FCSTD DOCUMENT  (FreeCAD 0.19R24291 (Git))
Label: drawer
License: All rights reserved
LicenseURL: http://en.wikipedia.org/wiki/All_rights_reserved
objects: App::Link×7, App::DocumentObjectGroup×2, PartDesign::CoordinateSystem×2, App::FeaturePython×2, App::Part×1
note: 2 computed .brp shape members not serialized (recipe doc carries the construction recipe); baked Part::Feature solids carry a one-line shape summary decoded from their .brp
EXTERNAL_REF file=InnerFrontWall.FCStd obj=LCS_0
EXTERNAL_REF file=InnerFrontWall.FCStd obj=InnerFrontWall
EXTERNAL_REF file=InnerFrontWall.FCStd obj=InnerFrontWall_InnerRightWall_
EXTERNAL_REF file=InnerRightWall.FCStd obj=LCS_0
EXTERNAL_REF file=InnerRightWall.FCStd obj=InnerRightWall
EXTERNAL_REF file=InnerFrontWall.FCStd obj=InnerFrontWall_OuterRightWall
EXTERNAL_REF file=OuterRightWall.FCStd obj=LCS_0
EXTERNAL_REF file=OuterRightWall.FCStd obj=OuterRightWall
EXTERNAL_REF file=BackWall.FCStd obj=LCS_0
EXTERNAL_REF file=BackWall.FCStd obj=BackWall
EXTERNAL_REF file=Bottom.FCStd obj=LCS_0
EXTERNAL_REF file=InnerFrontWall.FCStd obj=InnerFrontWall_Bottom
EXTERNAL_REF file=Bottom.FCStd obj=Bottom
EXTERNAL_REF file=InnerFrontWall.FCStd obj=InnerFrontWall_OuterFrontWall
EXTERNAL_REF file=OuterFrontWall.FCStd obj=LCS_0
EXTERNAL_REF file=OuterFrontWall.FCStd obj=OuterFrontWall
EXTERNAL_REF file=FrontWindow.FCStd obj=LCS_0
EXTERNAL_REF file=OuterFrontWall.FCStd obj=OuterFrontWall_FrontWindow
EXTERNAL_REF file=FrontWindow.FCStd obj=FrontWindow

FEATURE [App::DocumentObjectGroup] Parts
FEATURE [PartDesign::CoordinateSystem] LCS_Origin
  AttacherType = Attacher::AttachEngine3D
  MapMode = 2
  Support = -> [X_Axis]
FEATURE [App::DocumentObjectGroup] Constraints
FEATURE [App::FeaturePython] Variables  # WARN: FeaturePython — macro-defined, semantics opaque (R4)
FEATURE [App::Link] InnerFrontWall_InnerFrontWall
  AssemblyType = Asm4EE
  AttachedBy = #LCS_0
  AttachedTo = Parent Assembly#LCS_Origin
  LinkedObject = -> <external InnerFrontWall.FCStd>#InnerFrontWall
  expr: Placement = LCS_Origin.Placement * AttachmentOffset * InnerFrontWall#LCS_0.Placement ^ -1
FEATURE [App::Link] InnerRightWall_InnerRightWall
  AssemblyType = Asm4EE
  AttachedBy = #LCS_0
  AttachedTo = InnerFrontWall_InnerFrontWall#InnerFrontWall_InnerRightWall_
  LinkPlacement = pos=(380.8,-7.5,0) rot=(0,0,1;0rad)
  LinkedObject = -> <external InnerRightWall.FCStd>#InnerRightWall
  Placement = pos=(380.8,-7.5,0) rot=(0,0,1;0rad)
  expr: Placement = InnerFrontWall_InnerFrontWall.Placement * InnerFrontWall#InnerFrontWall_InnerRightWall_.Placement * AttachmentOffset * InnerRightWall#LCS_0.Placement ^ -1
FEATURE [App::Link] OuterRightWall_OuterRightWall
  AssemblyType = Asm4EE
  AttachedBy = #LCS_0
  AttachedTo = InnerFrontWall_InnerFrontWall#InnerFrontWall_OuterRightWall
  LinkPlacement = pos=(395.8,-7.5,0) rot=(0,0,1;0rad)
  LinkedObject = -> <external OuterRightWall.FCStd>#OuterRightWall
  Placement = pos=(395.8,-7.5,0) rot=(0,0,1;0rad)
  expr: Placement = InnerFrontWall_InnerFrontWall.Placement * InnerFrontWall#InnerFrontWall_OuterRightWall.Placement * AttachmentOffset * OuterRightWall#LCS_0.Placement ^ -1
FEATURE [PartDesign::CoordinateSystem] Temp_Back
  AttacherType = Attacher::AttachEngine3D
  AttachmentOffset = pos=(7.5,350.8,0) rot=(0,0,1;0rad)
  MapMode = 2
  Placement = pos=(7.5,350.8,0) rot=(0,0,1;0rad)
  Support = -> [LCS_Origin]
  expr: .AttachmentOffset.Base.x = <<Attributes>>.WallThickness_WT / 2
  expr: .AttachmentOffset.Base.y = <<Attributes>>.InnerWallDepth - <<Attributes>>.WallThickness_WT / 2
FEATURE [App::FeaturePython] PropertyBag  label="Attributes"  # WARN: FeaturePython — macro-defined, semantics opaque (R4)
  BackWidth = 395.8
  Back_Space = 104
  BottomDepth = 365.8
  BottomWidth = 365.8
  Bottom_Height_BH = 4
  Bottom_Space_Height = 20
  Box_Tolerance = 0.2
  Boxes_Depth = 5
  Boxes_Height = 40
  Boxes_Width = 5
  CableChannelHight = 15
  CableChannelRadius = 2
  CustomPropertyGroups = shape | attributes
  DrawerDepth_DD = 469.8
  DrawerHeight_DH = 64
  DrawerWidth_DW = 410.8
  InnerWallDepth = 358.3
  LogicBoardScrewHeadDiameter = 6
  LogicBoardScrewHeadHeight = 3
  LogicBoardStandoffHoleDiameter = 3
  LogicBoardStandoffHoleSideSpace = 6
  LogicSpaceCornerRadius = 2
  LogicSpaceWidth = 100
  ScrewPreWhole = 3
  ScrewPreWholeDepth = 20
  SideLengt = 20
  WallThickness_WT = 15
  expr: InnerWallDepth = Boxes_Depth * 70mm + WallThickness_WT * 0.5 + Box_Tolerance * (Boxes_Width - 1)
  expr: DrawerDepth_DD = Boxes_Depth * 70mm + WallThickness_WT + Back_Space + Box_Tolerance * (Boxes_Width - 1)
  expr: BottomWidth = Boxes_Width * 70mm + WallThickness_WT + Box_Tolerance * (Boxes_Width - 1)
  expr: DrawerWidth_DW = Boxes_Width * 70mm + WallThickness_WT * 4 + Box_Tolerance * (Boxes_Width - 1)
  expr: BackWidth = DrawerWidth_DW - WallThickness_WT
  expr: DrawerHeight_DH = Boxes_Height + Bottom_Height_BH + Bottom_Space_Height
  expr: BottomDepth = Boxes_Depth * 70mm + WallThickness_WT + Box_Tolerance * (Boxes_Width - 1)
FEATURE [App::Link] BackWall_BackWall
  AssemblyType = Asm4EE
  AttachedBy = #LCS_0
  AttachedTo = Parent Assembly#Temp_Back
  LinkPlacement = pos=(7.5,350.8,0) rot=(0,0,1;0rad)
  LinkedObject = -> <external BackWall.FCStd>#BackWall
  Placement = pos=(7.5,350.8,0) rot=(0,0,1;0rad)
  expr: Placement = Temp_Back.Placement * AttachmentOffset * BackWall#LCS_0.Placement ^ -1
FEATURE [App::Link] Bottom_Bottom
  AssemblyType = Asm4EE
  AttachedBy = #LCS_0
  AttachedTo = InnerFrontWall_InnerFrontWall#InnerFrontWall_Bottom
  LinkPlacement = pos=(22.5,-7.5,20) rot=(0,0,1;0rad)
  LinkedObject = -> <external Bottom.FCStd>#Bottom
  Placement = pos=(22.5,-7.5,20) rot=(0,0,1;0rad)
  expr: Placement = InnerFrontWall_InnerFrontWall.Placement * InnerFrontWall#InnerFrontWall_Bottom.Placement * AttachmentOffset * Bottom#LCS_0.Placement ^ -1
FEATURE [App::Link] OuterFrontWall_OuterFrontWall
  AssemblyType = Asm4EE
  AttachedBy = #LCS_0
  AttachedTo = InnerFrontWall_InnerFrontWall#InnerFrontWall_OuterFrontWall
  LinkPlacement = pos=(-20,-15,8.3e-15) rot=(0,0,1;0rad)
  LinkedObject = -> <external OuterFrontWall.FCStd>#OuterFrontWall
  Placement = pos=(-20,-15,8.3e-15) rot=(0,0,1;0rad)
  expr: Placement = InnerFrontWall_InnerFrontWall.Placement * InnerFrontWall#InnerFrontWall_OuterFrontWall.Placement * AttachmentOffset * OuterFrontWall#LCS_0.Placement ^ -1
FEATURE [App::Link] FrontWindow_FrontWindow
  AssemblyType = Asm4EE
  AttachedBy = #LCS_0
  AttachedTo = OuterFrontWall_OuterFrontWall#OuterFrontWall_FrontWindow
  LinkPlacement = pos=(329.8,-30,32) rot=(0,0,1;0rad)
  LinkedObject = -> <external FrontWindow.FCStd>#FrontWindow
  Placement = pos=(329.8,-30,32) rot=(0,0,1;0rad)
  expr: Placement = OuterFrontWall_OuterFrontWall.Placement * OuterFrontWall#OuterFrontWall_FrontWindow.Placement * AttachmentOffset * FrontWindow#LCS_0.Placement ^ -1
FEATURE [App::Part] Model
  Configuration = 0
  Group = -> [LCS_Origin,Constraints,Variables,InnerFrontWall_InnerFrontWall,InnerRightWall_InnerRightWall,OuterRightWall_OuterRightWall,Temp_Back,PropertyBag,BackWall_BackWall,Bottom_Bottom,OuterFrontWall_OuterFrontWall,FrontWindow_FrontWindow]
  Origin = -> Origin
  Type = Assembly4 Model

RESOLVED EXTERNAL PARTS (link-assembly join: the EXTERNAL_REF files above that resolve inside this repo's crawl, each included once):
---- part BackWall.FCStd = doc fcstd_9a13f263e70f ----
FCSTD DOCUMENT  (FreeCAD 0.19R24291 (Git))
Label: BackWall
License: All rights reserved
LicenseURL: http://en.wikipedia.org/wiki/All_rights_reserved
objects: Sketcher::SketchObject×6, PartDesign::Pocket×5, PartDesign::CoordinateSystem×2, PartDesign::Pad×1, App::FeaturePython×1, PartDesign::Body×1, App::Part×1
note: 21 computed .brp shape members not serialized (recipe doc carries the construction recipe); baked Part::Feature solids carry a one-line shape summary decoded from their .brp

FEATURE [PartDesign::CoordinateSystem] LCS_0
  AttacherType = Attacher::AttachEngine3D
  MapMode = 2
  Support = -> [X_Axis]
FEATURE [PartDesign::CoordinateSystem] LCS_0001
  AttacherType = Attacher::AttachEngine3D
  MapMode = 2
  Support = -> [X_Axis001]
FEATURE [Sketcher::SketchObject] Sketch
  FullyConstrained = true
  MapMode = 5
  Placement = pos=(0,0,0) rot=(1,0,0;1.5708rad)
  Support = -> [XZ_Plane001]
  expr: Constraints[9] = <<Attributes>>.BackWidth
  expr: Constraints[10] = <<Attributes>>.DrawerHeight_DH
  sketch-geometry (4):
    g0: LineSegment StartX=0 StartY=0 StartZ=0 EndX=395.8 EndY=0 EndZ=0
    g1: LineSegment StartX=395.8 StartY=0 StartZ=0 EndX=395.8 EndY=64 EndZ=0
    g2: LineSegment StartX=395.8 StartY=64 StartZ=0 EndX=0 EndY=64 EndZ=0
    g3: LineSegment StartX=0 StartY=64 StartZ=0 EndX=0 EndY=0 EndZ=0
  constraints (11):
    c: Coincident(g0,g1)
    c: Coincident(g1,g2)
    c: Coincident(g2,g3)
    c: Coincident(g3,g0)
    c: Horizontal(g0)
    c: Horizontal(g2)
    c: Vertical(g1)
    c: Vertical(g3)
    c: Coincident(g0,g-1)
    c: Distance(g2) = 395.8
    c: Distance(g3) = 64
FEATURE [PartDesign::Pad] Pad
  Direction = (1,1,1)
  Length = 15
  Length2 = 100
  Placement = pos=(0,0,0) rot=(1,0,0;1.5708rad)
  Profile = -> Sketch
  Reversed = true
  Type = 0
  expr: Length = <<Attributes>>.WallThickness_WT
FEATURE [Sketcher::SketchObject] Sketch001
  FullyConstrained = true
  MapMode = 5
  Placement = pos=(0,-1e-16,0) rot=(1,0,0;1.5708rad)
  Support = -> [Pad]
  expr: Constraints[2] = <<Attributes>>.WallThickness_WT * 1
  expr: Constraints[3] = <<Attributes>>.BackWidth - <<Attributes>>.WallThickness_WT * 2
  expr: Constraints[28] = <<Attributes>>.Bottom_Space_Height / 2
  expr: Constraints[21] = <<Attributes>>.ScrewPreWhole / 2
  expr: Constraints[14] = <<Attributes>>.DrawerHeight_DH - <<Attributes>>.WallThickness_WT - <<Attributes>>.Bottom_Space_Height - <<Attributes>>.Bottom_Height_BH
  expr: Constraints[33] = <<Attributes>>.DrawerHeight_DH - <<Attributes>>.WallThickness_WT / 2
  sketch-geometry (13):
    g0: LineSegment StartX=15 StartY=56.5 StartZ=0 EndX=380.8 EndY=56.5 EndZ=0
    g1: LineSegment StartX=380.8 StartY=31.5 StartZ=0 EndX=15 EndY=31.5 EndZ=0
    g2: LineSegment StartX=15 StartY=31.5 StartZ=0 EndX=15 EndY=44 EndZ=0
    g3: LineSegment StartX=15 StartY=44 StartZ=0 EndX=15 EndY=56.5 EndZ=0
    g4: LineSegment StartX=380.8 StartY=31.5 StartZ=0 EndX=380.8 EndY=44 EndZ=0
    g5: LineSegment StartX=380.8 StartY=44 StartZ=0 EndX=380.8 EndY=56.5 EndZ=0
    g6: Circle CenterX=15 CenterY=56.5 CenterZ=0 NormalX=0 NormalY=0 NormalZ=1 AngleXU=0 Radius=1.5
    g7: Circle CenterX=15 CenterY=31.5 CenterZ=0 NormalX=0 NormalY=0 NormalZ=1 AngleXU=0 Radius=1.5
    g8: Circle CenterX=380.8 CenterY=31.5 CenterZ=0 NormalX=0 NormalY=0 NormalZ=1 AngleXU=0 Radius=1.5
    g9: Circle CenterX=380.8 CenterY=56.5 CenterZ=0 NormalX=0 NormalY=0 NormalZ=1 AngleXU=0 Radius=1.5
    g10: LineSegment StartX=15 StartY=10 StartZ=0 EndX=380.8 EndY=10 EndZ=0
    g11: Circle CenterX=15 CenterY=10 CenterZ=0 NormalX=0 NormalY=0 NormalZ=1 AngleXU=0 Radius=1.5
    g12: Circle CenterX=380.8 CenterY=10 CenterZ=0 NormalX=0 NormalY=0 NormalZ=1 AngleXU=0 Radius=1.5
  constraints (34):
    c: Horizontal(g0)
    c: Horizontal(g1)
    c: DistanceX(g-1,g1) = 15
    c: Distance(g0) = 365.8
    c: Coincident(g1,g2)
    c: Vertical(g2)
    c: Coincident(g3,g0)
    c: Vertical(g3)
    c: Equal(g2,g3)
    c: Coincident(g1,g4)
    c: Vertical(g4)
    c: Coincident(g5,g0)
    c: Vertical(g5)
    c: Equal(g5,g4)
    c: Distance(g1,g0) = 25
    c: Coincident(g6,g0)
    c: Coincident(g7,g1)
    c: Coincident(g8,g1)
    c: Coincident(g9,g0)
    c: Equal(g9,g8)
    c: Equal(g8,g6)
    c: Radius(g6) = 1.5
    c: Coincident(g3,g2)
    c: Coincident(g4,g5)
    c: Equal(g7,g6)
    c: Horizontal(g10)
    c: Vertical(g7,g10)
    c: Equal(g10,g1)
    c: DistanceY(g-1,g10) = 10
    c: Coincident(g11,g10)
    c: Coincident(g12,g10)
    c: Equal(g8,g12)
    c: Equal(g12,g11)
    c: DistanceY(g-1,g6) = 56.5
FEATURE [PartDesign::Pocket] Pocket
  BaseFeature = -> Pad
  Length = 5
  Length2 = 100
  Placement = pos=(0,0,0) rot=(1,0,0;1.5708rad)
  Profile = -> Sketch001
  Type = 1
FEATURE [Sketcher::SketchObject] Sketch002
  FullyConstrained = true
  MapMode = 5
  Placement = pos=(0,-1e-16,0) rot=(1,0,0;1.5708rad)
  Support = -> [Pocket]
  expr: Constraints[9] = <<Attributes>>.BackWidth
  expr: Constraints[10] = <<Attributes>>.Bottom_Space_Height
  expr: Constraints[11] = <<Attributes>>.Bottom_Height_BH
  sketch-geometry (4):
    g0: LineSegment StartX=0 StartY=20 StartZ=0 EndX=395.8 EndY=20 EndZ=0
    g1: LineSegment StartX=395.8 StartY=20 StartZ=0 EndX=395.8 EndY=24 EndZ=0
    g2: LineSegment StartX=395.8 StartY=24 StartZ=0 EndX=0 EndY=24 EndZ=0
    g3: LineSegment StartX=0 StartY=24 StartZ=0 EndX=0 EndY=20 EndZ=0
  constraints (12):
    c: Coincident(g0,g1)
    c: Coincident(g1,g2)
    c: Coincident(g2,g3)
    c: Coincident(g3,g0)
    c: Horizontal(g0)
    c: Horizontal(g2)
    c: Vertical(g1)
    c: Vertical(g3)
    c: PointOnObject(g0,g-2)
    c: Distance(g2) = 395.8
    c: DistanceY(g-1,g0) = 20
    c: Distance(g3) = 4
FEATURE [PartDesign::Pocket] Pocket001
  BaseFeature = -> Pocket
  Length = 7.5
  Length2 = 100
  Placement = pos=(0,0,0) rot=(1,0,0;1.5708rad)
  Profile = -> Sketch002
  Type = 0
  expr: Length = <<Attributes>>.WallThickness_WT / 2
FEATURE [Sketcher::SketchObject] Sketch003
  FullyConstrained = true
  MapMode = 5
  Placement = pos=(395.8,0,0) rot=(0.707107,0,0.707107;3.14159rad)
  Support = -> [Pocket001]
  expr: Constraints[3] = <<Attributes>>.WallThickness_WT / 2
  expr: Constraints[4] = <<Attributes>>.DrawerHeight_DH - <<Attributes>>.WallThickness_WT / 2
  expr: Constraints[5] = <<Attributes>>.Bottom_Space_Height / 2
  expr: Constraints[6] = <<Attributes>>.DrawerHeight_DH - <<Attributes>>.WallThickness_WT - <<Attributes>>.Bottom_Space_Height - <<Attributes>>.Bottom_Height_BH
  expr: Constraints[12] = <<Attributes>>.ScrewPreWhole / 2
  sketch-geometry (5):
    g0: LineSegment StartX=10 StartY=-7.5 StartZ=0 EndX=31.5 EndY=-7.5 EndZ=0
    g1: LineSegment StartX=31.5 StartY=-7.5 StartZ=0 EndX=56.5 EndY=-7.5 EndZ=0
    g2: Circle CenterX=10 CenterY=-7.5 CenterZ=0 NormalX=0 NormalY=0 NormalZ=1 AngleXU=0 Radius=1.5
    g3: Circle CenterX=31.5 CenterY=-7.5 CenterZ=0 NormalX=0 NormalY=0 NormalZ=1 AngleXU=0 Radius=1.5
    g4: Circle CenterX=56.5 CenterY=-7.5 CenterZ=0 NormalX=0 NormalY=0 NormalZ=1 AngleXU=0 Radius=1.5
  constraints (13):
    c: Horizontal(g0)
    c: Coincident(g0,g1)
    c: Horizontal(g1)
    c: DistanceY(g0,g-1) = 7.5
    c: DistanceX(g-1,g1) = 56.5
    c: DistanceX(g-1,g0) = 10
    c: Distance(g1) = 25
    c: Coincident(g2,g0)
    c: Coincident(g3,g0)
    c: Coincident(g4,g1)
    c: Equal(g2,g3)
    c: Equal(g3,g4)
    c: Radius(g2) = 1.5
FEATURE [PartDesign::Pocket] Pocket002
  BaseFeature = -> Pocket001
  Length = 20
  Length2 = 100
  Placement = pos=(0,0,0) rot=(1,0,0;1.5708rad)
  Profile = -> Sketch003
  Type = 0
  expr: Length = <<Attributes>>.ScrewPreWholeDepth
FEATURE [Sketcher::SketchObject] Sketch004
  FullyConstrained = true
  MapMode = 5
  Placement = pos=(0,0,0) rot=(0.707107,0,-0.707107;3.14159rad)
  Support = -> [Pocket002]
  expr: Constraints[3] = <<Attributes>>.WallThickness_WT / 2
  expr: Constraints[4] = <<Attributes>>.DrawerHeight_DH - <<Attributes>>.WallThickness_WT / 2
  expr: Constraints[5] = <<Attributes>>.DrawerHeight_DH - <<Attributes>>.WallThickness_WT - <<Attributes>>.Bottom_Space_Height - <<Attributes>>.Bottom_Height_BH
  expr: Constraints[6] = <<Attributes>>.Bottom_Space_Height / 2
  expr: Constraints[12] = <<Attributes>>.ScrewPreWhole / 2
  sketch-geometry (5):
    g0: LineSegment StartX=-10 StartY=-7.5 StartZ=0 EndX=-31.5 EndY=-7.5 EndZ=0
    g1: LineSegment StartX=-31.5 StartY=-7.5 StartZ=0 EndX=-56.5 EndY=-7.5 EndZ=0
    g2: Circle CenterX=-56.5 CenterY=-7.5 CenterZ=0 NormalX=0 NormalY=0 NormalZ=1 AngleXU=0 Radius=1.5
    g3: Circle CenterX=-31.5 CenterY=-7.5 CenterZ=0 NormalX=0 NormalY=0 NormalZ=1 AngleXU=0 Radius=1.5
    g4: Circle CenterX=-10 CenterY=-7.5 CenterZ=0 NormalX=0 NormalY=0 NormalZ=1 AngleXU=0 Radius=1.5
  constraints (13):
    c: Horizontal(g0)
    c: Coincident(g0,g1)
    c: Horizontal(g1)
    c: DistanceY(g0,g-1) = 7.5
    c: DistanceX(g1,g-1) = 56.5
    c: Distance(g1) = 25
    c: DistanceX(g0,g-1) = 10
    c: Coincident(g2,g1)
    c: Coincident(g3,g0)
    c: Coincident(g4,g0)
    c: Equal(g4,g3)
    c: Equal(g3,g2)
    c: Radius(g4) = 1.5
FEATURE [PartDesign::Pocket] Pocket003
  BaseFeature = -> Pocket002
  Length = 20
  Length2 = 100
  Placement = pos=(0,0,0) rot=(1,0,0;1.5708rad)
  Profile = -> Sketch004
  Type = 0
  expr: Length = <<Attributes>>.ScrewPreWholeDepth
FEATURE [Sketcher::SketchObject] Sketch005
  FullyConstrained = true
  MapMode = 5
  Placement = pos=(0,15,3.3e-15) rot=(-1,0,0;1.5708rad)
  Support = -> [Pocket003]
  expr: Constraints[42] = <<Attributes>>.CableChannelRadius
  expr: Constraints[41] = <<Attributes>>.DrawerHeight_DH - <<Attributes>>.WallThickness_WT / 2 - (<<Attributes>>.DrawerHeight_DH - <<Attributes>>.WallThickness_WT - <<Attributes>>.Bottom_Space_Height - <<Attributes>>.Bottom_Height_BH) / 2
  expr: Constraints[40] = <<Attributes>>.CableChannelHight
  expr: Constraints[10] = <<Attributes>>.DrawerWidth_DW - <<Attributes>>.WallThickness_WT
  expr: Constraints[30] = <<Attributes>>.WallThickness_WT
  sketch-geometry (17):
    g0: LineSegment StartX=0 StartY=-51.5 StartZ=0 EndX=13 EndY=-51.5 EndZ=0
    g1: LineSegment StartX=15 StartY=-49.5 StartZ=0 EndX=15 EndY=-38.5 EndZ=0
    g2: LineSegment StartX=13 StartY=-36.5 StartZ=0 EndX=0 EndY=-36.5 EndZ=0
    g3: LineSegment StartX=0 StartY=-36.5 StartZ=0 EndX=0 EndY=-51.5 EndZ=0
    g4: LineSegment StartX=395.8 StartY=-51.5 StartZ=0 EndX=382.8 EndY=-51.5 EndZ=0
    g5: LineSegment StartX=380.8 StartY=-49.5 StartZ=0 EndX=380.8 EndY=-38.5 EndZ=0
    g6: LineSegment StartX=382.8 StartY=-36.5 StartZ=0 EndX=395.8 EndY=-36.5 EndZ=0
    g7: ArcOfCircle CenterX=13 CenterY=-49.5 CenterZ=0 NormalX=0 NormalY=0 NormalZ=1 AngleXU=0 Radius=2 StartAngle=4.71239 EndAngle=6.28319
    g8: GeomPoint X=15 Y=-51.5 Z=0
    g9: ArcOfCircle CenterX=13 CenterY=-38.5 CenterZ=0 NormalX=0 NormalY=0 NormalZ=1 AngleXU=0 Radius=2 StartAngle=-9e-16 EndAngle=1.5708
    g10: GeomPoint X=15 Y=-36.5 Z=0
    g11: ArcOfCircle CenterX=382.8 CenterY=-49.5 CenterZ=0 NormalX=0 NormalY=0 NormalZ=1 AngleXU=0 Radius=2 StartAngle=3.14159 EndAngle=4.71239
    g12: GeomPoint X=380.8 Y=-51.5 Z=0
    g13: ArcOfCircle CenterX=382.8 CenterY=-38.5 CenterZ=0 NormalX=0 NormalY=0 NormalZ=1 AngleXU=0 Radius=2 StartAngle=1.5708 EndAngle=3.14159
    g14: GeomPoint X=380.8 Y=-36.5 Z=0
    g15: LineSegment StartX=395.8 StartY=-36.5 StartZ=0 EndX=395.8 EndY=-44 EndZ=0
    g16: LineSegment StartX=395.8 StartY=-44 StartZ=0 EndX=395.8 EndY=-51.5 EndZ=0
  constraints (43):
    c: Coincident(g2,g3)
    c: Coincident(g3,g0)
    c: Horizontal(g0)
    c: Horizontal(g2)
    c: Vertical(g1)
    c: Vertical(g3)
    c: PointOnObject(g0,g-2)
    c: Horizontal(g4)
    c: Horizontal(g6)
    c: Vertical(g5)
    c: DistanceX(g-1,g6) = 395.8
    c: PointOnObject(g8,g0)
    c: PointOnObject(g8,g1)
    c: Tangent(g0,g7) = -1.5708
    c: Tangent(g1,g7) = -1.5708
    c: PointOnObject(g10,g1)
    c: PointOnObject(g10,g2)
    c: Tangent(g1,g9) = -1.5708
    c: Tangent(g2,g9) = -1.5708
    c: PointOnObject(g12,g4)
    c: PointOnObject(g12,g5)
    c: Tangent(g4,g11) = 1.5708
    c: Tangent(g5,g11) = 1.5708
    c: PointOnObject(g14,g5)
    c: PointOnObject(g14,g6)
    c: Tangent(g5,g13) = 1.5708
    c: Tangent(g6,g13) = 1.5708
    c: Equal(g13,g11)
    c: Equal(g11,g7)
    c: Equal(g7,g9)
    c: DistanceX(g14,g6) = 15
    c: Equal(g2,g6)
    c: Horizontal(g8,g12)
    c: Coincident(g6,g15)
    c: Vertical(g15)
    c: Coincident(g15,g16)
    c: Coincident(g16,g4)
    c: Vertical(g16)
    c: Equal(g15,g16)
    c: Horizontal(g2,g6)
    c: DistanceY(g4,g6) = 15
    c: DistanceY(g15,g-1) = 44
    c: Radius(g13) = 2
FEATURE [App::FeaturePython] PropertyBag  label="Attributes"  # WARN: FeaturePython — macro-defined, semantics opaque (R4)
  BackWidth = 395.8
  Back_Space = 100
  BottomDepth = 365.8
  BottomWidth = 365.8
  Bottom_Height_BH = 4
  Bottom_Space_Height = 20
  Box_Tolerance = 0.2
  Boxes_Depth = 5
  Boxes_Height = 40
  Boxes_Width = 5
  CableChannelHight = 15
  CableChannelRadius = 2
  CustomPropertyGroups = shape | attributes
  DrawerDepth_DD = 465.8
  DrawerHeight_DH = 64
  DrawerWidth_DW = 410.8
  InnerWallDepth = 358.3
  LogicBoardScrewHeadDiameter = 6
  LogicBoardScrewHeadHeight = 3
  LogicBoardStandoffHoleDiameter = 3
  LogicBoardStandoffHoleSideSpace = 6
  LogicSpaceCornerRadius = 2
  LogicSpaceWidth = 100
  ScrewPreWhole = 3
  ScrewPreWholeDepth = 20
  SideLengt = 20
  WallThickness_WT = 15
  expr: InnerWallDepth = Boxes_Depth * 70mm + WallThickness_WT * 0.5 + Box_Tolerance * (Boxes_Width - 1)
  expr: DrawerDepth_DD = Boxes_Depth * 70mm + WallThickness_WT + Back_Space + Box_Tolerance * (Boxes_Width - 1)
  expr: BottomWidth = Boxes_Width * 70mm + WallThickness_WT + Box_Tolerance * (Boxes_Width - 1)
  expr: DrawerWidth_DW = Boxes_Width * 70mm + WallThickness_WT * 4 + Box_Tolerance * (Boxes_Width - 1)
  expr: BackWidth = DrawerWidth_DW - WallThickness_WT
  expr: DrawerHeight_DH = Boxes_Height + Bottom_Height_BH + Bottom_Space_Height
  expr: BottomDepth = Boxes_Depth * 70mm + WallThickness_WT + Box_Tolerance * (Boxes_Width - 1)
FEATURE [PartDesign::Pocket] Pocket004
  BaseFeature = -> Pocket003
  Length = 5
  Length2 = 100
  Placement = pos=(0,0,0) rot=(1,0,0;1.5708rad)
  Profile = -> Sketch005
  Type = 1
FEATURE [PartDesign::Body] BackWall001
  Group = -> [LCS_0001,Sketch,Pad,Sketch001,Pocket,Sketch002,Pocket001,Sketch003,Pocket002,Sketch004,Pocket003,Sketch005,Pocket004]
  Origin = -> Origin001
  Tip = -> Pocket004
FEATURE [App::Part] BackWall
  Group = -> [LCS_0,BackWall001,PropertyBag]
  Origin = -> Origin
---- part Bottom.FCStd = doc fcstd_1e701def4303 ----
FCSTD DOCUMENT  (FreeCAD 0.19R24291 (Git))
Label: Bottom
License: All rights reserved
LicenseURL: http://en.wikipedia.org/wiki/All_rights_reserved
objects: PartDesign::CoordinateSystem×2, Sketcher::SketchObject×2, PartDesign::LinearPattern×2, App::FeaturePython×1, PartDesign::Pad×1, PartDesign::Pocket×1, PartDesign::MultiTransform×1, PartDesign::Body×1, App::Part×1
note: 12 computed .brp shape members not serialized (recipe doc carries the construction recipe); baked Part::Feature solids carry a one-line shape summary decoded from their .brp

FEATURE [PartDesign::CoordinateSystem] LCS_0
  AttacherType = Attacher::AttachEngine3D
  MapMode = 2
  Support = -> [X_Axis]
FEATURE [PartDesign::CoordinateSystem] LCS_0001
  AttacherType = Attacher::AttachEngine3D
  MapMode = 2
  Support = -> [X_Axis001]
FEATURE [App::FeaturePython] PropertyBag  label="Attributes"  # WARN: FeaturePython — macro-defined, semantics opaque (R4)
  BackWidth = 395.8
  Back_Space = 100
  BottomDepth = 365.8
  BottomWidth = 365.8
  Bottom_Height_BH = 4
  Bottom_Space_Height = 20
  Box_Tolerance = 0.2
  Boxes_Depth = 5
  Boxes_Height = 40
  Boxes_Width = 5
  CustomPropertyGroups = shape | attributes
  DrawerDepth_DD = 465.8
  DrawerHeight_DH = 64
  DrawerWidth_DW = 410.8
  ScrewPreWhole = 3
  WallThickness_WT = 15
  expr: DrawerDepth_DD = Boxes_Depth * 70mm + WallThickness_WT + Back_Space + Box_Tolerance * (Boxes_Width - 1)
  expr: BottomWidth = Boxes_Width * 70mm + WallThickness_WT + Box_Tolerance * (Boxes_Width - 1)
  expr: DrawerWidth_DW = Boxes_Width * 70mm + WallThickness_WT * 4 + Box_Tolerance * (Boxes_Width - 1)
  expr: BackWidth = DrawerWidth_DW - WallThickness_WT
  expr: DrawerHeight_DH = Boxes_Height + Bottom_Height_BH + Bottom_Space_Height
  expr: BottomDepth = Boxes_Depth * 70mm + WallThickness_WT + Box_Tolerance * (Boxes_Width - 1)
FEATURE [Sketcher::SketchObject] Sketch
  FullyConstrained = true
  MapMode = 5
  Support = -> [XY_Plane001]
  expr: Constraints[9] = <<Attributes>>.BottomWidth
  expr: Constraints[10] = <<Attributes>>.BottomDepth
  sketch-geometry (4):
    g0: LineSegment StartX=0 StartY=0 StartZ=0 EndX=365.8 EndY=0 EndZ=0
    g1: LineSegment StartX=365.8 StartY=0 StartZ=0 EndX=365.8 EndY=365.8 EndZ=0
    g2: LineSegment StartX=365.8 StartY=365.8 StartZ=0 EndX=0 EndY=365.8 EndZ=0
    g3: LineSegment StartX=0 StartY=365.8 StartZ=0 EndX=0 EndY=0 EndZ=0
  constraints (11):
    c: Coincident(g0,g1)
    c: Coincident(g1,g2)
    c: Coincident(g2,g3)
    c: Coincident(g3,g0)
    c: Horizontal(g0)
    c: Horizontal(g2)
    c: Vertical(g1)
    c: Vertical(g3)
    c: Coincident(g0,g-1)
    c: Distance(g0) = 365.8
    c: Distance(g3) = 365.8
FEATURE [PartDesign::Pad] Pad
  Direction = (1,1,1)
  Length = 4
  Length2 = 100
  Profile = -> Sketch
  Type = 0
  expr: Length = <<Attributes>>.Bottom_Height_BH
FEATURE [Sketcher::SketchObject] Sketch001
  FullyConstrained = true
  MapMode = 5
  Placement = pos=(0,0,4) rot=(0,0,1;0rad)
  Support = -> [Pad]
  expr: Constraints[5] = 70mm + <<Attributes>>.Box_Tolerance / 2
  expr: Constraints[13] = <<Attributes>>.WallThickness_WT / 2
  expr: Constraints[14] = <<Attributes>>.WallThickness_WT / 2
  expr: Constraints[60] = 3mm + <<Attributes>>.Box_Tolerance
  expr: Constraints[6] = 70mm + <<Attributes>>.Box_Tolerance / 2
  expr: Constraints[59] = 10mm + <<Attributes>>.Box_Tolerance
  sketch-geometry (42):
    g0: LineSegment StartX=77.6 StartY=7.5 StartZ=0 EndX=77.6 EndY=77.6 EndZ=0
    g1: LineSegment StartX=77.6 StartY=77.6 StartZ=0 EndX=7.5 EndY=77.6 EndZ=0
    g2: LineSegment StartX=7.5 StartY=77.6 StartZ=0 EndX=7.5 EndY=7.5 EndZ=0
    g3: LineSegment StartX=7.5 StartY=7.5 StartZ=0 EndX=42.55 EndY=7.5 EndZ=0
    g4: LineSegment StartX=42.55 StartY=7.5 StartZ=0 EndX=77.6 EndY=7.5 EndZ=0
    g5: LineSegment StartX=7.5 StartY=77.6 StartZ=0 EndX=10.7 EndY=77.6 EndZ=0
    g6: LineSegment StartX=10.7 StartY=77.6 StartZ=0 EndX=10.7 EndY=67.4 EndZ=0
    g7: LineSegment StartX=10.7 StartY=67.4 StartZ=0 EndX=7.5 EndY=67.4 EndZ=0
    g8: LineSegment StartX=7.5 StartY=7.5 StartZ=0 EndX=10.7 EndY=7.5 EndZ=0
    g9: LineSegment StartX=10.7 StartY=7.5 StartZ=0 EndX=10.7 EndY=17.7 EndZ=0
    g10: LineSegment StartX=10.7 StartY=17.7 StartZ=0 EndX=7.5 EndY=17.7 EndZ=0
    g11: LineSegment StartX=77.6 StartY=77.6 StartZ=0 EndX=74.4 EndY=77.6 EndZ=0
    g12: LineSegment StartX=74.4 StartY=77.6 StartZ=0 EndX=74.4 EndY=67.4 EndZ=0
    g13: LineSegment StartX=74.4 StartY=67.4 StartZ=0 EndX=77.6 EndY=67.4 EndZ=0
    g14: LineSegment StartX=77.6 StartY=7.5 StartZ=0 EndX=74.4 EndY=7.5 EndZ=0
    g15: LineSegment StartX=74.4 StartY=7.5 StartZ=0 EndX=74.4 EndY=17.7 EndZ=0
    g16: LineSegment StartX=74.4 StartY=17.7 StartZ=0 EndX=77.6 EndY=17.7 EndZ=0
    g17: LineSegment StartX=37.45 StartY=10.7 StartZ=0 EndX=47.65 EndY=10.7 EndZ=0
    g18: LineSegment StartX=47.65 StartY=10.7 StartZ=0 EndX=47.65 EndY=7.5 EndZ=0
    g19: LineSegment StartX=37.45 StartY=7.5 StartZ=0 EndX=37.45 EndY=10.7 EndZ=0
    g20: LineSegment StartX=37.45 StartY=7.5 StartZ=0 EndX=42.55 EndY=7.5 EndZ=0
    g21: LineSegment StartX=42.55 StartY=7.5 StartZ=0 EndX=47.65 EndY=7.5 EndZ=0
    g22: LineSegment StartX=7.5 StartY=7.5 StartZ=0 EndX=7.5 EndY=12.6 EndZ=0
    g23: LineSegment StartX=7.5 StartY=12.6 StartZ=0 EndX=7.5 EndY=17.7 EndZ=0
    g24: LineSegment StartX=77.6 StartY=7.5 StartZ=0 EndX=77.6 EndY=12.6 EndZ=0
    g25: LineSegment StartX=77.6 StartY=12.6 StartZ=0 EndX=77.6 EndY=17.7 EndZ=0
    g26: LineSegment StartX=77.6 StartY=77.6 StartZ=0 EndX=77.6 EndY=72.5 EndZ=0
    g27: LineSegment StartX=77.6 StartY=72.5 StartZ=0 EndX=77.6 EndY=67.4 EndZ=0
    g28: LineSegment StartX=7.5 StartY=67.4 StartZ=0 EndX=7.5 EndY=72.5 EndZ=0
    g29: LineSegment StartX=7.5 StartY=72.5 StartZ=0 EndX=7.5 EndY=77.6 EndZ=0
    g30: Circle CenterX=22.5 CenterY=12.6 CenterZ=0 NormalX=0 NormalY=0 NormalZ=1 AngleXU=0 Radius=1.5
    g31: Circle CenterX=42.55 CenterY=22.5 CenterZ=0 NormalX=0 NormalY=0 NormalZ=1 AngleXU=0 Radius=1.5
    g32: Circle CenterX=22.5 CenterY=72.5 CenterZ=0 NormalX=0 NormalY=0 NormalZ=1 AngleXU=0 Radius=1.5
    g33: Circle CenterX=62.6 CenterY=72.5 CenterZ=0 NormalX=0 NormalY=0 NormalZ=1 AngleXU=0 Radius=1
    g34: Circle CenterX=62.6 CenterY=12.6 CenterZ=0 NormalX=0 NormalY=0 NormalZ=1 AngleXU=0 Radius=1
    g35: LineSegment StartX=7.5 StartY=12.6 StartZ=0 EndX=22.5 EndY=12.6 EndZ=0
    g36: LineSegment StartX=7.5 StartY=72.5 StartZ=0 EndX=22.5 EndY=72.5 EndZ=0
    g37: LineSegment StartX=77.6 StartY=72.5 StartZ=0 EndX=62.6 EndY=72.5 EndZ=0
    g38: LineSegment StartX=42.55 StartY=7.5 StartZ=0 EndX=42.55 EndY=22.5 EndZ=0
    g39: LineSegment StartX=77.6 StartY=12.6 StartZ=0 EndX=62.6 EndY=12.6 EndZ=0
    g40: LineSegment StartX=42.55 StartY=77.6 StartZ=0 EndX=42.55 EndY=62.6 EndZ=0
    g41: Circle CenterX=42.55 CenterY=62.6 CenterZ=0 NormalX=0 NormalY=0 NormalZ=1 AngleXU=0 Radius=1
  constraints (116):
    c: Coincident(g0,g1)
    c: Coincident(g1,g2)
    c: Horizontal(g1)
    c: Vertical(g0)
    c: Vertical(g2)
    c: Distance(g2) = 70.1
    c: Distance(g1) = 70.1
    c: Coincident(g2,g3)
    c: Horizontal(g3)
    c: Coincident(g3,g4)
    c: Coincident(g4,g0)
    c: Horizontal(g4)
    c: Equal(g3,g4)
    c: DistanceY(g-1,g2) = 7.5
    c: DistanceX(g-1,g2) = 7.5
    c: Coincident(g5,g6)
    c: Coincident(g6,g7)
    c: Horizontal(g5)
    c: Horizontal(g7)
    c: Vertical(g6)
    c: Coincident(g5,g1)
    c: Coincident(g8,g9)
    c: Coincident(g9,g10)
    c: Horizontal(g8)
    c: Horizontal(g10)
    c: Vertical(g9)
    c: Coincident(g8,g2)
    c: Coincident(g11,g12)
    c: Coincident(g12,g13)
    c: Horizontal(g11)
    c: Horizontal(g13)
    c: Vertical(g12)
    c: Coincident(g11,g0)
    c: Coincident(g14,g15)
    c: Coincident(g15,g16)
    c: Horizontal(g14)
    c: Horizontal(g16)
    c: Vertical(g15)
    c: Coincident(g14,g0)
    c: Coincident(g17,g18)
    c: Coincident(g19,g17)
    c: Horizontal(g17)
    c: Vertical(g18)
    c: Vertical(g19)
    c: Coincident(g19,g20)
    c: Horizontal(g20)
    c: Coincident(g20,g21)
    c: Coincident(g21,g18)
    c: Horizontal(g21)
    c: Equal(g20,g21)
    c: Equal(g17,g15)
    c: Equal(g15,g9)
    c: Equal(g9,g6)
    c: Equal(g6,g12)
    c: Coincident(g3,g20)
    c: Equal(g19,g10)
    c: Equal(g10,g7)
    c: Equal(g7,g13)
    c: Equal(g13,g16)
    c: Distance(g9) = 10.2
    c: Distance(g10) = 3.2
    c: Coincident(g8,g22)
    c: Vertical(g22)
    c: Coincident(g22,g23)
    c: Coincident(g23,g10)
    c: Vertical(g23)
    c: Equal(g23,g22)
    c: Coincident(g14,g24)
    c: Vertical(g24)
    c: Coincident(g24,g25)
    c: Coincident(g25,g16)
    c: Vertical(g25)
    c: Coincident(g11,g26)
    c: Vertical(g26)
    c: Coincident(g26,g27)
    c: Coincident(g27,g13)
    c: Vertical(g27)
    c: Coincident(g7,g28)
    c: Vertical(g28)
    c: Coincident(g28,g29)
    c: Coincident(g29,g5)
    c: Vertical(g29)
    c: Equal(g29,g28)
    c: Equal(g26,g27)
    c: Equal(g24,g25)
    c: Coincident(g35,g22)
    c: Coincident(g35,g30)
    c: Horizontal(g35)
    c: Coincident(g36,g28)
    c: Coincident(g36,g32)
    c: Coincident(g37,g26)
    c: Coincident(g37,g33)
    c: Coincident(g38,g20)
    c: Coincident(g38,g31)
    c: Coincident(g39,g24)
    c: Coincident(g39,g34)
    c: Horizontal(g39)
    c: Horizontal(g37)
    c: Horizontal(g36)
    c: Vertical(g38)
    c: Equal(g30,g32)
    c: Equal(g33,g34)
    c: Radius(g32) = 1.5
    c: Radius(g33) = 1
    c: PointOnObject(g40,g1)
    c: Vertical(g40)
    c: Coincident(g41,g40)
    c: Equal(g41,g33)
    c: Equal(g32,g31)
    c: Vertical(g41,g31)
    c: Equal(g40,g37)
    c: Equal(g40,g36)
    c: Equal(g36,g35)
    c: Equal(g35,g38)
    c: Equal(g38,g39)
    c: Distance(g35) = 15
FEATURE [PartDesign::Pocket] Pocket
  BaseFeature = -> Pad
  Length = 5
  Length2 = 100
  Profile = -> Sketch001
  Type = 1
FEATURE [PartDesign::LinearPattern] LinearPattern
  Direction = -> Sketch001 [H_Axis]
  Length = 280.4
  Occurrences = 5
  expr: Length = (<<Attributes>>.Boxes_Width - 1) * (70mm + <<Attributes>>.Box_Tolerance / 2)
  expr: Occurrences = <<Attributes>>.Boxes_Width
FEATURE [PartDesign::LinearPattern] LinearPattern001
  Direction = -> Y_Axis001
  Length = 280.4
  Occurrences = 5
  expr: Length = (<<Attributes>>.Boxes_Depth - 1) * (70mm + <<Attributes>>.Box_Tolerance / 2)
  expr: Occurrences = <<Attributes>>.Boxes_Depth
FEATURE [PartDesign::MultiTransform] MultiTransform
  BaseFeature = -> Pocket
  Originals = -> [Pocket]
  Transformations = -> [LinearPattern,LinearPattern001]
FEATURE [PartDesign::Body] Bottom001
  Group = -> [LCS_0001,Sketch,Pad,Sketch001,Pocket,MultiTransform,LinearPattern,LinearPattern001]
  Origin = -> Origin001
  Tip = -> MultiTransform
FEATURE [App::Part] Bottom
  Group = -> [LCS_0,Bottom001,PropertyBag]
  Origin = -> Origin
---- part FrontWindow.FCStd = doc fcstd_6366f4dbabd7 ----
FCSTD DOCUMENT  (FreeCAD 0.19R24291 (Git))
Label: FrontWindow
License: All rights reserved
LicenseURL: http://en.wikipedia.org/wiki/All_rights_reserved
objects: PartDesign::CoordinateSystem×2, Sketcher::SketchObject×2, App::FeaturePython×1, PartDesign::Pad×1, PartDesign::Pocket×1, PartDesign::Body×1, App::Part×1
note: 9 computed .brp shape members not serialized (recipe doc carries the construction recipe); baked Part::Feature solids carry a one-line shape summary decoded from their .brp

FEATURE [PartDesign::CoordinateSystem] LCS_0
  AttacherType = Attacher::AttachEngine3D
  MapMode = 2
  Support = -> [X_Axis]
FEATURE [PartDesign::CoordinateSystem] LCS_0001
  AttacherType = Attacher::AttachEngine3D
  MapMode = 2
  Support = -> [X_Axis001]
FEATURE [Sketcher::SketchObject] Sketch
  FullyConstrained = true
  MapMode = 5
  Placement = pos=(0,0,0) rot=(1,0,0;1.5708rad)
  Support = -> [XZ_Plane001]
  expr: Constraints[31] = <<Attributes>>.LogicSpaceCornerRadius
  expr: Constraints[5] = <<Attributes>>.DrawerHeight_DH - <<Attributes>>.WallThickness_WT / 4 - <<Attributes>>.WallThickness_WT / 4
  expr: Constraints[4] = <<Attributes>>.DrawerWidth_DW + <<Attributes>>.SideLengt * 2 - (<<Attributes>>.SideLengt + <<Attributes>>.WallThickness_WT * 2 + <<Attributes>>.LogicSpaceCornerRadius) + <<Attributes>>.WallThickness_WT / 4 - (<<Attributes>>.DrawerWidth_DW + <<Attributes>>.SideLengt * 2 - (<<Attributes>>.SideLengt + <<Attributes>>.WallThickness_WT * 2 + <<Attributes>>.LogicSpaceCornerRadius + <<Attributes>>.LogicSpaceWidth) - <<Attributes>>.WallThickness_WT / 4)
  sketch-geometry (14):
    g0: LineSegment StartX=-52.75 StartY=28.25 StartZ=0 EndX=52.75 EndY=28.25 EndZ=0
    g1: LineSegment StartX=53.75 StartY=27.25 StartZ=0 EndX=53.75 EndY=-27.25 EndZ=0
    g2: LineSegment StartX=52.75 StartY=-28.25 StartZ=0 EndX=-52.75 EndY=-28.25 EndZ=0
    g3: LineSegment StartX=-53.75 StartY=-27.25 StartZ=0 EndX=-53.75 EndY=27.25 EndZ=0
    g4: ArcOfCircle CenterX=-52.75 CenterY=27.25 CenterZ=0 NormalX=0 NormalY=0 NormalZ=1 AngleXU=0 Radius=1 StartAngle=1.5708 EndAngle=3.14159
    g5: GeomPoint X=-53.75 Y=28.25 Z=0
    g6: ArcOfCircle CenterX=52.75 CenterY=27.25 CenterZ=0 NormalX=0 NormalY=0 NormalZ=1 AngleXU=0 Radius=1 StartAngle=-2.84e-14 EndAngle=1.5708
    g7: GeomPoint X=53.75 Y=28.25 Z=0
    g8: ArcOfCircle CenterX=52.75 CenterY=-27.25 CenterZ=0 NormalX=0 NormalY=0 NormalZ=1 AngleXU=0 Radius=1 StartAngle=4.71239 EndAngle=6.28319
    g9: GeomPoint X=53.75 Y=-28.25 Z=0
    g10: ArcOfCircle CenterX=-52.75 CenterY=-27.25 CenterZ=0 NormalX=0 NormalY=0 NormalZ=1 AngleXU=0 Radius=1 StartAngle=3.14159 EndAngle=4.71239
    g11: GeomPoint X=-53.75 Y=-28.25 Z=0
    g12: LineSegment StartX=-52.75 StartY=-27.25 StartZ=0 EndX=52.75 EndY=27.25 EndZ=0
    g13: LineSegment StartX=-52.75 StartY=27.25 StartZ=0 EndX=52.75 EndY=-27.25 EndZ=0
  constraints (32):
    c: Horizontal(g0)
    c: Horizontal(g2)
    c: Vertical(g1)
    c: Vertical(g3)
    c: Distance(g7,g5) = 107.5
    c: Distance(g11,g5) = 56.5
    c: PointOnObject(g5,g0)
    c: PointOnObject(g5,g3)
    c: Tangent(g0,g4) = 1.5708
    c: Tangent(g3,g4) = 1.5708
    c: PointOnObject(g7,g0)
    c: PointOnObject(g7,g1)
    c: Tangent(g0,g6) = 1.5708
    c: Tangent(g1,g6) = 1.5708
    c: PointOnObject(g9,g1)
    c: PointOnObject(g9,g2)
    c: Tangent(g1,g8) = 1.5708
    c: Tangent(g2,g8) = 1.5708
    c: PointOnObject(g11,g2)
    c: PointOnObject(g11,g3)
    c: Tangent(g2,g10) = 1.5708
    c: Tangent(g3,g10) = 1.5708
    c: Coincident(g12,g10)
    c: Coincident(g12,g6)
    c: Coincident(g13,g4)
    c: Coincident(g13,g8)
    c: PointOnObject(g-1,g13)
    c: PointOnObject(g-1,g12)
    c: Equal(g6,g4)
    c: Equal(g4,g10)
    c: Equal(g10,g8)
    c: Radius(g6) = 1
FEATURE [App::FeaturePython] PropertyBag  label="Attributes"  # WARN: FeaturePython — macro-defined, semantics opaque (R4)
  BackWidth = 395.8
  Back_Space = 100
  BottomDepth = 365.8
  BottomWidth = 365.8
  Bottom_Height_BH = 4
  Bottom_Space_Height = 20
  Box_Tolerance = 0.2
  Boxes_Depth = 5
  Boxes_Height = 40
  Boxes_Width = 5
  CableChannelHight = 15
  CableChannelRadius = 2
  CustomPropertyGroups = shape | attributes
  DrawerDepth_DD = 465.8
  DrawerHeight_DH = 64
  DrawerWidth_DW = 410.8
  FrontWindowRecessedDepth = 3
  FrontWindowThickness = 6
  HandelDimA = 100
  HandelDimB = 30
  HandelDimC = 140
  HandelDimD = 70
  HandelDimE = 30
  InnerWallDepth = 358.3
  LogicBoardScrewHeadDiameter = 6
  LogicBoardScrewHeadHeight = 3
  LogicBoardStandoffHoleDiameter = 3
  LogicBoardStandoffHoleSideSpace = 6
  LogicSpaceCornerRadius = 1
  LogicSpaceWidth = 100
  ScrewPreWhole = 3
  ScrewPreWholeDepth = 20
  SideLengt = 20
  WallThickness_WT = 15
  expr: InnerWallDepth = Boxes_Depth * 70mm + WallThickness_WT * 0.5 + Box_Tolerance * (Boxes_Width - 1)
  expr: DrawerDepth_DD = Boxes_Depth * 70mm + WallThickness_WT + Back_Space + Box_Tolerance * (Boxes_Width - 1)
  expr: BottomWidth = Boxes_Width * 70mm + WallThickness_WT + Box_Tolerance * (Boxes_Width - 1)
  expr: DrawerWidth_DW = Boxes_Width * 70mm + WallThickness_WT * 4 + Box_Tolerance * (Boxes_Width - 1)
  expr: BackWidth = DrawerWidth_DW - WallThickness_WT
  expr: DrawerHeight_DH = Boxes_Height + Bottom_Height_BH + Bottom_Space_Height
  expr: BottomDepth = Boxes_Depth * 70mm + WallThickness_WT + Box_Tolerance * (Boxes_Width - 1)
FEATURE [PartDesign::Pad] Pad
  Direction = (1,1,1)
  Length = 6
  Length2 = 100
  Placement = pos=(0,0,0) rot=(1,0,0;1.5708rad)
  Profile = -> Sketch
  Reversed = true
  Type = 0
  expr: Length = <<Attributes>>.FrontWindowThickness
FEATURE [Sketcher::SketchObject] Sketch001
  FullyConstrained = true
  MapMode = 5
  Placement = pos=(0,0,0) rot=(1,0,0;1.5708rad)
  Support = -> [XZ_Plane001]
  expr: Constraints[47] = (<<Attributes>>.DrawerHeight_DH - <<Attributes>>.WallThickness_WT / 2 - <<Attributes>>.WallThickness_WT / 2) * 1.5
  expr: Constraints[46] = <<Attributes>>.LogicSpaceWidth * 1.5
  expr: Constraints[25] = <<Attributes>>.LogicSpaceCornerRadius
  expr: Constraints[5] = <<Attributes>>.LogicSpaceWidth
  expr: Constraints[4] = <<Attributes>>.DrawerHeight_DH - <<Attributes>>.WallThickness_WT / 2 - <<Attributes>>.WallThickness_WT / 2
  sketch-geometry (20):
    g0: LineSegment StartX=-49 StartY=24.5 StartZ=0 EndX=49 EndY=24.5 EndZ=0
    g1: LineSegment StartX=50 StartY=23.5 StartZ=0 EndX=50 EndY=-23.5 EndZ=0
    g2: LineSegment StartX=49 StartY=-24.5 StartZ=0 EndX=-49 EndY=-24.5 EndZ=0
    g3: LineSegment StartX=-50 StartY=-23.5 StartZ=0 EndX=-50 EndY=23.5 EndZ=0
    g4: ArcOfCircle CenterX=-49 CenterY=23.5 CenterZ=0 NormalX=0 NormalY=0 NormalZ=1 AngleXU=0 Radius=1 StartAngle=1.5708 EndAngle=3.14159
    g5: GeomPoint X=-50 Y=24.5 Z=0
    g6: ArcOfCircle CenterX=49 CenterY=23.5 CenterZ=0 NormalX=0 NormalY=0 NormalZ=1 AngleXU=0 Radius=1 StartAngle=1.1e-15 EndAngle=1.5708
    g7: GeomPoint X=50 Y=24.5 Z=0
    g8: ArcOfCircle CenterX=49 CenterY=-23.5 CenterZ=0 NormalX=0 NormalY=0 NormalZ=1 AngleXU=0 Radius=1 StartAngle=4.71239 EndAngle=6.28319
    g9: GeomPoint X=50 Y=-24.5 Z=0
    g10: ArcOfCircle CenterX=-49 CenterY=-23.5 CenterZ=0 NormalX=0 NormalY=0 NormalZ=1 AngleXU=0 Radius=1 StartAngle=3.14159 EndAngle=4.71239
    g11: GeomPoint X=-50 Y=-24.5 Z=0
    g12: LineSegment StartX=-49 StartY=23.5 StartZ=0 EndX=49 EndY=-23.5 EndZ=0
    g13: LineSegment StartX=49 StartY=23.5 StartZ=0 EndX=-49 EndY=-23.5 EndZ=0
    g14: LineSegment StartX=-75 StartY=36.75 StartZ=0 EndX=75 EndY=36.75 EndZ=0
    g15: LineSegment StartX=75 StartY=36.75 StartZ=0 EndX=75 EndY=-36.75 EndZ=0
    g16: LineSegment StartX=75 StartY=-36.75 StartZ=0 EndX=-75 EndY=-36.75 EndZ=0
    g17: LineSegment StartX=-75 StartY=-36.75 StartZ=0 EndX=-75 EndY=36.75 EndZ=0
    g18: LineSegment StartX=-75 StartY=36.75 StartZ=0 EndX=75 EndY=-36.75 EndZ=0
    g19: LineSegment StartX=-75 StartY=-36.75 StartZ=0 EndX=75 EndY=36.75 EndZ=0
  constraints (48):
    c: Horizontal(g0)
    c: Horizontal(g2)
    c: Vertical(g1)
    c: Vertical(g3)
    c: DistanceY(g11,g5) = 49
    c: DistanceX(g5,g7) = 100
    c: PointOnObject(g5,g0)
    c: PointOnObject(g5,g3)
    c: Tangent(g0,g4) = 1.5708
    c: Tangent(g3,g4) = 1.5708
    c: PointOnObject(g7,g0)
    c: PointOnObject(g7,g1)
    c: Tangent(g0,g6) = 1.5708
    c: Tangent(g1,g6) = 1.5708
    c: PointOnObject(g9,g1)
    c: PointOnObject(g9,g2)
    c: Tangent(g1,g8) = 1.5708
    c: Tangent(g2,g8) = 1.5708
    c: PointOnObject(g11,g2)
    c: PointOnObject(g11,g3)
    c: Tangent(g2,g10) = 1.5708
    c: Tangent(g3,g10) = 1.5708
    c: Equal(g6,g4)
    c: Equal(g4,g10)
    c: Equal(g10,g8)
    c: Radius(g6) = 1
    c: Coincident(g12,g4)
    c: Coincident(g12,g8)
    c: Coincident(g13,g6)
    c: Coincident(g13,g10)
    c: PointOnObject(g-1,g12)
    c: PointOnObject(g-1,g13)
    c: Coincident(g14,g15)
    c: Coincident(g15,g16)
    c: Coincident(g16,g17)
    c: Coincident(g17,g14)
    c: Horizontal(g14)
    c: Horizontal(g16)
    c: Vertical(g15)
    c: Vertical(g17)
    c: Coincident(g18,g14)
    c: Coincident(g18,g15)
    c: Coincident(g19,g16)
    c: Coincident(g19,g14)
    c: PointOnObject(g-1,g18)
    c: PointOnObject(g-1,g19)
    c: Distance(g14) = 150
    c: Distance(g17) = 73.5
FEATURE [PartDesign::Pocket] Pocket
  BaseFeature = -> Pad
  Length = 3
  Length2 = 100
  Placement = pos=(0,0,0) rot=(1,0,0;1.5708rad)
  Profile = -> Sketch001
  Type = 0
  expr: Length = <<Attributes>>.FrontWindowRecessedDepth
FEATURE [PartDesign::Body] FrontWindow001
  Group = -> [LCS_0001,Sketch,Pad,Sketch001,Pocket]
  Origin = -> Origin001
  Tip = -> Pocket
FEATURE [App::Part] FrontWindow
  Group = -> [LCS_0,FrontWindow001,PropertyBag]
  Origin = -> Origin
---- part InnerFrontWall.FCStd = doc fcstd_5a2104c4ae9e ----
FCSTD DOCUMENT  (FreeCAD 0.19R24291 (Git))
Label: InnerFrontWall
License: All rights reserved
LicenseURL: http://en.wikipedia.org/wiki/All_rights_reserved
objects: PartDesign::CoordinateSystem×10, Sketcher::SketchObject×9, PartDesign::Pocket×8, PartDesign::Plane×2, App::FeaturePython×1, PartDesign::Pad×1, PartDesign::Body×1, App::Part×1
note: 40 computed .brp shape members not serialized (recipe doc carries the construction recipe); baked Part::Feature solids carry a one-line shape summary decoded from their .brp

FEATURE [PartDesign::CoordinateSystem] LCS_0
  AttacherType = Attacher::AttachEngine3D
  MapMode = 2
  Support = -> [X_Axis]
FEATURE [PartDesign::CoordinateSystem] LCS_0001
  AttacherType = Attacher::AttachEngine3D
  MapMode = 2
  Support = -> [X_Axis001]
FEATURE [Sketcher::SketchObject] Sketch
  FullyConstrained = true
  MapMode = 5
  Placement = pos=(0,0,0) rot=(1,0,0;1.5708rad)
  Support = -> [XZ_Plane001]
  expr: Constraints[4] = <<Attributes>>.DrawerHeight_DH
  expr: Constraints[7] = <<Attributes>>.SideLengt * 2 + <<Attributes>>.DrawerWidth_DW
  expr: Constraints[11] = <<Attributes>>.SideLengt
  sketch-geometry (4):
    g0: LineSegment StartX=430.8 StartY=0 StartZ=0 EndX=430.8 EndY=64 EndZ=0
    g1: LineSegment StartX=430.8 StartY=64 StartZ=0 EndX=-20 EndY=64 EndZ=0
    g2: LineSegment StartX=-20 StartY=64 StartZ=0 EndX=-20 EndY=0 EndZ=0
    g3: LineSegment StartX=-20 StartY=0 StartZ=0 EndX=430.8 EndY=0 EndZ=0
  constraints (12):
    c: Vertical(g0)
    c: Horizontal(g1)
    c: Horizontal(g3)
    c: Vertical(g2)
    c: Distance(g2) = 64
    c: Coincident(g1,g0)
    c: Coincident(g1,g2)
    c: Distance(g1) = 450.8
    c: Coincident(g3,g0)
    c: Coincident(g2,g3)
    c: PointOnObject(g2,g-1)
    c: DistanceX(g2,g-1) = 20
FEATURE [App::FeaturePython] PropertyBag  label="Attributes"  # WARN: FeaturePython — macro-defined, semantics opaque (R4)
  BackWidth = 395.8
  Back_Space = 100
  BottomDepth = 365.8
  BottomWidth = 365.8
  Bottom_Height_BH = 4
  Bottom_Space_Height = 20
  Box_Tolerance = 0.2
  Boxes_Depth = 5
  Boxes_Height = 40
  Boxes_Width = 5
  CableChannelHight = 15
  CableChannelRadius = 2
  CustomPropertyGroups = shape | attributes
  DrawerDepth_DD = 465.8
  DrawerHeight_DH = 64
  DrawerWidth_DW = 410.8
  InnerWallDepth = 358.3
  LogicBoardScrewHeadDiameter = 6
  LogicBoardScrewHeadHeight = 3
  LogicBoardStandoffHoleDiameter = 3
  LogicBoardStandoffHoleSideSpace = 6
  LogicSpaceCornerRadius = 1
  LogicSpaceWidth = 100
  ScrewPreWhole = 3
  ScrewPreWholeDepth = 20
  SideLengt = 20
  WallThickness_WT = 15
  expr: InnerWallDepth = Boxes_Depth * 70mm + WallThickness_WT * 0.5 + Box_Tolerance * (Boxes_Width - 1)
  expr: DrawerDepth_DD = Boxes_Depth * 70mm + WallThickness_WT + Back_Space + Box_Tolerance * (Boxes_Width - 1)
  expr: BottomWidth = Boxes_Width * 70mm + WallThickness_WT + Box_Tolerance * (Boxes_Width - 1)
  expr: DrawerWidth_DW = Boxes_Width * 70mm + WallThickness_WT * 4 + Box_Tolerance * (Boxes_Width - 1)
  expr: BackWidth = DrawerWidth_DW - WallThickness_WT
  expr: DrawerHeight_DH = Boxes_Height + Bottom_Height_BH + Bottom_Space_Height
  expr: BottomDepth = Boxes_Depth * 70mm + WallThickness_WT + Box_Tolerance * (Boxes_Width - 1)
FEATURE [PartDesign::Pad] Pad
  Direction = (1,1,1)
  Length = 15
  Length2 = 100
  Placement = pos=(0,0,0) rot=(1,0,0;1.5708rad)
  Profile = -> Sketch
  Type = 0
  expr: Length = <<Attributes>>.WallThickness_WT
FEATURE [PartDesign::Plane] DatumPlane
  Length = 60
  MapMode = 3
  Placement = pos=(0,0,0) rot=(1,0,0;1.5708rad)
  ResizeMode = 0
  Support = -> [LCS_0]
  Width = 60
FEATURE [Sketcher::SketchObject] Sketch001
  FullyConstrained = true
  MapMode = 5
  Placement = pos=(0,0,0) rot=(1,0,0;1.5708rad)
  Support = -> [DatumPlane]
  expr: Constraints[12] = <<Attributes>>.WallThickness_WT * 2
  expr: Constraints[13] = <<Attributes>>.DrawerWidth_DW
  expr: Constraints[19] = <<Attributes>>.DrawerWidth_DW - <<Attributes>>.WallThickness_WT * 4
  expr: Constraints[20] = <<Attributes>>.DrawerHeight_DH
  sketch-geometry (8):
    g0: LineSegment StartX=0 StartY=0 StartZ=0 EndX=30 EndY=0 EndZ=0
    g1: LineSegment StartX=30 StartY=64 StartZ=0 EndX=0 EndY=64 EndZ=0
    g2: LineSegment StartX=0 StartY=64 StartZ=0 EndX=0 EndY=0 EndZ=0
    g3: LineSegment StartX=380.8 StartY=0 StartZ=0 EndX=410.8 EndY=0 EndZ=0
    g4: LineSegment StartX=410.8 StartY=0 StartZ=0 EndX=410.8 EndY=64 EndZ=0
    g5: LineSegment StartX=410.8 StartY=64 StartZ=0 EndX=380.8 EndY=64 EndZ=0
    g6: LineSegment StartX=380.8 StartY=64 StartZ=0 EndX=380.8 EndY=0 EndZ=0
    g7: LineSegment StartX=30 StartY=0 StartZ=0 EndX=30 EndY=64 EndZ=0
  constraints (23):
    c: Coincident(g1,g2)
    c: Coincident(g2,g0)
    c: Horizontal(g0)
    c: Horizontal(g1)
    c: Vertical(g2)
    c: Coincident(g0,g-1)
    c: Coincident(g3,g4)
    c: Coincident(g4,g5)
    c: Horizontal(g3)
    c: Horizontal(g5)
    c: Vertical(g4)
    c: PointOnObject(g3,g-1)
    c: Distance(g0) = 30
    c: DistanceX(g0,g3) = 410.8
    c: Coincident(g5,g6)
    c: Vertical(g6)
    c: Coincident(g7,g1)
    c: Vertical(g7)
    c: Equal(g6,g7)
    c: DistanceX(g0,g3) = 350.8
    c: Distance(g2) = 64
    c: Coincident(g7,g0)
    c: Coincident(g6,g3)
FEATURE [PartDesign::Pocket] Pocket
  BaseFeature = -> Pad
  Length = 7.5
  Length2 = 100
  Placement = pos=(0,0,0) rot=(1,0,0;1.5708rad)
  Profile = -> Sketch001
  Reversed = true
  Type = 0
  expr: Length = <<Attributes>>.WallThickness_WT / 2
FEATURE [PartDesign::Plane] DatumPlane001
  AttachmentOffset = pos=(0,0,15) rot=(0,0,1;0rad)
  Length = 60
  MapMode = 3
  Placement = pos=(0,-15,3.3e-15) rot=(1,0,0;1.5708rad)
  ResizeMode = 0
  Support = -> [LCS_0]
  Width = 60
  expr: .AttachmentOffset.Base.z = <<Attributes>>.WallThickness_WT
FEATURE [Sketcher::SketchObject] Sketch002
  FullyConstrained = true
  MapMode = 5
  Placement = pos=(0,-15,3.3e-15) rot=(1,0,0;1.5708rad)
  Support = -> [DatumPlane001]
  expr: Constraints[48] = <<Attributes>>.LogicSpaceWidth
  expr: Constraints[49] = <<Attributes>>.DrawerHeight_DH - <<Attributes>>.WallThickness_WT / 2 - (<<Attributes>>.DrawerHeight_DH - <<Attributes>>.WallThickness_WT - <<Attributes>>.Bottom_Space_Height - <<Attributes>>.Bottom_Height_BH) / 2
  expr: Constraints[20] = <<Attributes>>.CableChannelHight
  expr: Constraints[10] = <<Attributes>>.LogicSpaceCornerRadius
  expr: Constraints[2] = <<Attributes>>.DrawerWidth_DW
  expr: Constraints[50] = <<Attributes>>.LogicSpaceCornerRadius * 2
  expr: Constraints[51] = <<Attributes>>.DrawerHeight_DH - <<Attributes>>.WallThickness_WT / 2
  expr: Constraints[1] = <<Attributes>>.WallThickness_WT / 2
  expr: Constraints[38] = <<Attributes>>.WallThickness_WT * 2
  sketch-geometry (24):
    g0: LineSegment StartX=279.8 StartY=55.5 StartZ=0 EndX=279.8 EndY=8.5 EndZ=0
    g1: ArcOfCircle CenterX=409.8 CenterY=50.5 CenterZ=0 NormalX=0 NormalY=0 NormalZ=1 AngleXU=0 Radius=1 StartAngle=1.5e-15 EndAngle=1.5708
    g2: GeomPoint X=410.8 Y=51.5 Z=0
    g3: ArcOfCircle CenterX=280.8 CenterY=55.5 CenterZ=0 NormalX=0 NormalY=0 NormalZ=1 AngleXU=0 Radius=1 StartAngle=1.5708 EndAngle=3.14159
    g4: GeomPoint X=279.8 Y=56.5 Z=0
    g5: ArcOfCircle CenterX=280.8 CenterY=8.5 CenterZ=0 NormalX=0 NormalY=0 NormalZ=1 AngleXU=0 Radius=1 StartAngle=3.14159 EndAngle=4.71239
    g6: GeomPoint X=279.8 Y=7.5 Z=0
    g7: ArcOfCircle CenterX=409.8 CenterY=37.5 CenterZ=0 NormalX=0 NormalY=0 NormalZ=1 AngleXU=0 Radius=1 StartAngle=4.71239 EndAngle=6.28317
    g8: GeomPoint X=410.8 Y=36.5 Z=0
    g9: LineSegment StartX=410.8 StartY=37.5 StartZ=0 EndX=410.8 EndY=44 EndZ=0
    g10: LineSegment StartX=410.8 StartY=44 StartZ=0 EndX=410.8 EndY=50.5 EndZ=0
    g11: LineSegment StartX=409.8 StartY=51.5 StartZ=0 EndX=380.8 EndY=51.5 EndZ=0
    g12: LineSegment StartX=378.8 StartY=56.5 StartZ=0 EndX=280.8 EndY=56.5 EndZ=0
    g13: LineSegment StartX=280.8 StartY=7.5 StartZ=0 EndX=378.8 EndY=7.5 EndZ=0
    g14: LineSegment StartX=379.8 StartY=8.5 StartZ=0 EndX=379.8 EndY=35.5 EndZ=0
    g15: LineSegment StartX=380.8 StartY=36.5 StartZ=0 EndX=409.8 EndY=36.5 EndZ=0
    g16: ArcOfCircle CenterX=380.8 CenterY=35.5 CenterZ=0 NormalX=0 NormalY=0 NormalZ=1 AngleXU=0 Radius=1 StartAngle=1.5708 EndAngle=3.14159
    g17: GeomPoint X=379.8 Y=36.5 Z=0
    g18: GeomPoint X=378.8 Y=56.5 Z=0
    g19: ArcOfCircle CenterX=378.8 CenterY=8.5 CenterZ=0 NormalX=0 NormalY=0 NormalZ=1 AngleXU=0 Radius=1 StartAngle=4.71239 EndAngle=6.28319
    g20: GeomPoint X=379.8 Y=7.5 Z=0
    g21: ArcOfCircle CenterX=378.8 CenterY=55.5 CenterZ=0 NormalX=0 NormalY=0 NormalZ=1 AngleXU=0 Radius=1 StartAngle=-1.8e-15 EndAngle=1.5708
    g22: ArcOfCircle CenterX=380.8 CenterY=52.5 CenterZ=0 NormalX=0 NormalY=0 NormalZ=1 AngleXU=0 Radius=1 StartAngle=3.14159 EndAngle=4.71239
    g23: LineSegment StartX=379.8 StartY=55.5 StartZ=0 EndX=379.8 EndY=52.5 EndZ=0
  constraints (62):
    c: Vertical(g0)
    c: DistanceY(g-1,g6) = 7.5
    c: DistanceX(g-1,g2) = 410.8
    c: PointOnObject(g4,g0)
    c: Tangent(g0,g3) = -1.5708
    c: PointOnObject(g6,g0)
    c: Tangent(g0,g5) = -1.5708
    c: Equal(g3,g1)
    c: Equal(g1,g7)
    c: Equal(g7,g5)
    c: Radius(g3) = 1
    c: Horizontal(g7,g8)
    c: Horizontal(g1,g2)
    c: Vertical(g1,g2)
    c: Vertical(g7,g8)
    c: Coincident(g9,g10)
    c: Vertical(g9)
    c: Vertical(g10)
    c: Tangent(g10,g1) = -1.5708
    c: Equal(g9,g10)
    c: DistanceY(g7,g1) = 15
    c: Vertical(g1,g1)
    c: Vertical(g1,g7)
    c: Tangent(g1,g11) = -1.5708
    c: Horizontal(g12)
    c: Tangent(g5,g13) = -1.5708
    c: Vertical(g14)
    c: Coincident(g15,g7)
    c: Horizontal(g15)
    c: PointOnObject(g17,g14)
    c: PointOnObject(g17,g15)
    c: Tangent(g14,g16) = 1.5708
    c: Tangent(g15,g16) = 1.5708
    c: PointOnObject(g20,g13)
    c: PointOnObject(g20,g14)
    c: Tangent(g13,g19) = -1.5708
    c: Tangent(g14,g19) = -1.5708
    c: Equal(g19,g16)
    c: DistanceX(g11,g1) = 30
    c: Tangent(g12,g3) = -1.5708
    c: Horizontal(g13)
    c: Horizontal(g5,g6)
    c: Horizontal(g3,g4)
    c: Coincident(g9,g7)
    c: Vertical(g7,g1)
    c: Vertical(g11,g15)
    c: Equal(g16,g5)
    c: Coincident(g18,g12)
    c: DistanceX(g0,g14) = 100
    c: DistanceY(g-1,g9) = 44
    c: DistanceX(g12,g11) = 2
    c: DistanceY(g-1,g3) = 56.5
    c: Coincident(g21,g12)
    c: Coincident(g22,g11)
    c: Coincident(g23,g21)
    c: Coincident(g23,g22)
    c: Equal(g22,g21)
    c: Equal(g21,g3)
    c: Angle(g22) = 1.5708
    c: Angle(g21) = 1.5708
    c: Vertical(g21,g12)
    c: Horizontal(g22,g22)
FEATURE [PartDesign::Pocket] Pocket001
  BaseFeature = -> Pocket
  Length = 3.75
  Length2 = 100
  Placement = pos=(0,0,0) rot=(1,0,0;1.5708rad)
  Profile = -> Sketch002
  Type = 0
  expr: Length = <<Attributes>>.WallThickness_WT / 4
FEATURE [Sketcher::SketchObject] Sketch003
  FullyConstrained = true
  MapMode = 5
  Placement = pos=(0,-15,3.3e-15) rot=(1,0,0;1.5708rad)
  Support = -> [DatumPlane001]
  expr: Constraints[19] = <<Attributes>>.LogicSpaceCornerRadius
  expr: Constraints[15] = <<Attributes>>.DrawerWidth_DW
  expr: Constraints[20] = <<Attributes>>.CableChannelHight
  expr: Constraints[26] = <<Attributes>>.DrawerHeight_DH - <<Attributes>>.WallThickness_WT / 2 - (<<Attributes>>.DrawerHeight_DH - <<Attributes>>.WallThickness_WT - <<Attributes>>.Bottom_Space_Height - <<Attributes>>.Bottom_Height_BH) / 2
  expr: Constraints[29] = <<Attributes>>.WallThickness_WT * 2
  sketch-geometry (13):
    g0: LineSegment StartX=381.8 StartY=51.5 StartZ=0 EndX=409.8 EndY=51.5 EndZ=0
    g1: LineSegment StartX=410.8 StartY=50.5 StartZ=0 EndX=410.8 EndY=37.5 EndZ=0
    g2: LineSegment StartX=409.8 StartY=36.5 StartZ=0 EndX=381.8 EndY=36.5 EndZ=0
    g3: ArcOfCircle CenterX=381.8 CenterY=50.5 CenterZ=0 NormalX=0 NormalY=0 NormalZ=1 AngleXU=0 Radius=1 StartAngle=1.5708 EndAngle=3.14159
    g4: GeomPoint X=380.8 Y=51.5 Z=0
    g5: ArcOfCircle CenterX=409.8 CenterY=50.5 CenterZ=0 NormalX=0 NormalY=0 NormalZ=1 AngleXU=0 Radius=1 StartAngle=-3.6e-15 EndAngle=1.5708
    g6: GeomPoint X=410.8 Y=51.5 Z=0
    g7: ArcOfCircle CenterX=381.8 CenterY=37.5 CenterZ=0 NormalX=0 NormalY=0 NormalZ=1 AngleXU=0 Radius=1 StartAngle=3.14159 EndAngle=4.71239
    g8: GeomPoint X=380.8 Y=36.5 Z=0
    g9: ArcOfCircle CenterX=409.8 CenterY=37.5 CenterZ=0 NormalX=0 NormalY=0 NormalZ=1 AngleXU=0 Radius=1 StartAngle=4.71239 EndAngle=6.28319
    g10: GeomPoint X=410.8 Y=36.5 Z=0
    g11: LineSegment StartX=380.8 StartY=37.5 StartZ=0 EndX=380.8 EndY=44 EndZ=0
    g12: LineSegment StartX=380.8 StartY=44 StartZ=0 EndX=380.8 EndY=50.5 EndZ=0
  constraints (31):
    c: Horizontal(g0)
    c: Horizontal(g2)
    c: Vertical(g1)
    c: PointOnObject(g4,g0)
    c: Tangent(g0,g3) = 1.5708
    c: PointOnObject(g6,g0)
    c: PointOnObject(g6,g1)
    c: Tangent(g0,g5) = 1.5708
    c: Tangent(g1,g5) = 1.5708
    c: PointOnObject(g8,g2)
    c: Tangent(g2,g7) = 1.5708
    c: PointOnObject(g10,g1)
    c: PointOnObject(g10,g2)
    c: Tangent(g1,g9) = 1.5708
    c: Tangent(g2,g9) = 1.5708
    c: DistanceX(g-1,g6) = 410.8
    c: Equal(g5,g3)
    c: Equal(g3,g7)
    c: Equal(g7,g9)
    c: Radius(g5) = 1
    c: DistanceY(g10,g6) = 15
    c: Tangent(g7,g11) = 1.5708
    c: Coincident(g11,g12)
    c: Vertical(g12)
    c: Vertical(g11)
    c: Equal(g11,g12)
    c: DistanceY(g-1,g11) = 44
    c: Vertical(g3,g4)
    c: Tangent(g12,g3) = 1.5708
    c: DistanceX(g4,g6) = 30
    c: Vertical(g8,g7)
FEATURE [PartDesign::Pocket] Pocket002
  BaseFeature = -> Pocket001
  Length = 5
  Length2 = 100
  Placement = pos=(0,0,0) rot=(1,0,0;1.5708rad)
  Profile = -> Sketch003
  Type = 1
FEATURE [Sketcher::SketchObject] Sketch005
  FullyConstrained = true
  MapMode = 5
  Placement = pos=(0,-15,3.3e-15) rot=(1,0,0;1.5708rad)
  Support = -> [DatumPlane001]
  expr: Constraints[5] = <<Attributes>>.WallThickness_WT / 2
  expr: Constraints[6] = <<Attributes>>.DrawerHeight_DH - <<Attributes>>.WallThickness_WT / 2
  expr: Constraints[39] = <<Attributes>>.LogicBoardStandoffHoleSideSpace + <<Attributes>>.LogicBoardStandoffHoleDiameter / 2
  expr: Constraints[7] = <<Attributes>>.DrawerWidth_DW - <<Attributes>>.WallThickness_WT * 2 - <<Attributes>>.LogicSpaceCornerRadius
  expr: Constraints[27] = <<Attributes>>.LogicSpaceCornerRadius
  expr: Constraints[4] = <<Attributes>>.LogicSpaceWidth
  expr: Constraints[32] = <<Attributes>>.LogicBoardStandoffHoleSideSpace + <<Attributes>>.LogicBoardStandoffHoleDiameter / 2
  expr: Constraints[38] = <<Attributes>>.LogicBoardStandoffHoleSideSpace + <<Attributes>>.LogicBoardStandoffHoleDiameter / 2
  expr: Constraints[31] = <<Attributes>>.LogicBoardStandoffHoleDiameter / 2
  expr: Constraints[33] = <<Attributes>>.LogicBoardStandoffHoleSideSpace + <<Attributes>>.LogicBoardStandoffHoleDiameter / 2
  expr: Constraints[34] = <<Attributes>>.LogicBoardStandoffHoleSideSpace + <<Attributes>>.LogicBoardStandoffHoleDiameter / 2
  expr: Constraints[36] = <<Attributes>>.LogicBoardStandoffHoleSideSpace + <<Attributes>>.LogicBoardStandoffHoleDiameter / 2
  expr: Constraints[35] = <<Attributes>>.LogicBoardStandoffHoleSideSpace + <<Attributes>>.LogicBoardStandoffHoleDiameter / 2
  expr: Constraints[37] = <<Attributes>>.LogicBoardStandoffHoleSideSpace + <<Attributes>>.LogicBoardStandoffHoleDiameter / 2
  sketch-geometry (16):
    g0: LineSegment StartX=280.8 StartY=56.5 StartZ=0 EndX=378.8 EndY=56.5 EndZ=0
    g1: LineSegment StartX=379.8 StartY=55.5 StartZ=0 EndX=379.8 EndY=8.5 EndZ=0
    g2: LineSegment StartX=378.8 StartY=7.5 StartZ=0 EndX=280.8 EndY=7.5 EndZ=0
    g3: LineSegment StartX=279.8 StartY=8.5 StartZ=0 EndX=279.8 EndY=55.5 EndZ=0
    g4: ArcOfCircle CenterX=280.8 CenterY=55.5 CenterZ=0 NormalX=0 NormalY=0 NormalZ=1 AngleXU=0 Radius=1 StartAngle=1.5708 EndAngle=3.14159
    g5: GeomPoint X=279.8 Y=56.5 Z=0
    g6: ArcOfCircle CenterX=280.8 CenterY=8.5 CenterZ=0 NormalX=0 NormalY=0 NormalZ=1 AngleXU=0 Radius=1 StartAngle=3.14159 EndAngle=4.71239
    g7: GeomPoint X=279.8 Y=7.5 Z=0
    g8: ArcOfCircle CenterX=378.8 CenterY=8.5 CenterZ=0 NormalX=0 NormalY=0 NormalZ=1 AngleXU=0 Radius=1 StartAngle=4.71239 EndAngle=6.28319
    g9: GeomPoint X=379.8 Y=7.5 Z=0
    g10: ArcOfCircle CenterX=378.8 CenterY=55.5 CenterZ=0 NormalX=0 NormalY=0 NormalZ=1 AngleXU=0 Radius=1 StartAngle=1.2e-15 EndAngle=1.5708
    g11: GeomPoint X=379.8 Y=56.5 Z=0
    g12: Circle CenterX=287.3 CenterY=49 CenterZ=0 NormalX=0 NormalY=0 NormalZ=1 AngleXU=0 Radius=1.5
    g13: Circle CenterX=287.3 CenterY=15 CenterZ=0 NormalX=0 NormalY=0 NormalZ=1 AngleXU=0 Radius=1.5
    g14: Circle CenterX=372.3 CenterY=49 CenterZ=0 NormalX=0 NormalY=0 NormalZ=1 AngleXU=0 Radius=1.5
    g15: Circle CenterX=372.3 CenterY=15 CenterZ=0 NormalX=0 NormalY=0 NormalZ=1 AngleXU=0 Radius=1.5
  constraints (40):
    c: Horizontal(g0)
    c: Horizontal(g2)
    c: Vertical(g1)
    c: Vertical(g3)
    c: DistanceX(g5,g11) = 100
    c: DistanceY(g-1,g7) = 7.5
    c: DistanceY(g-1,g5) = 56.5
    c: DistanceX(g-1,g11) = 379.8
    c: PointOnObject(g5,g0)
    c: PointOnObject(g5,g3)
    c: Tangent(g0,g4) = 1.5708
    c: Tangent(g3,g4) = 1.5708
    c: PointOnObject(g7,g2)
    c: PointOnObject(g7,g3)
    c: Tangent(g2,g6) = 1.5708
    c: Tangent(g3,g6) = 1.5708
    c: PointOnObject(g9,g1)
    c: PointOnObject(g9,g2)
    c: Tangent(g1,g8) = 1.5708
    c: Tangent(g2,g8) = 1.5708
    c: PointOnObject(g11,g0)
    c: PointOnObject(g11,g1)
    c: Tangent(g0,g10) = 1.5708
    c: Tangent(g1,g10) = 1.5708
    c: Equal(g4,g6)
    c: Equal(g6,g8)
    c: Equal(g8,g10)
    c: Radius(g4) = 1
    c: Equal(g12,g14)
    c: Equal(g14,g15)
    c: Equal(g15,g13)
    c: Radius(g12) = 1.5
    c: DistanceX(g14,g1) = 7.5
    c: DistanceY(g14,g0) = 7.5
    c: DistanceX(g3,g12) = 7.5
    c: DistanceY(g12,g0) = 7.5
    c: DistanceX(g3,g13) = 7.5
    c: DistanceY(g2,g13) = 7.5
    c: DistanceY(g2,g15) = 7.5
    c: DistanceX(g15,g1) = 7.5
FEATURE [PartDesign::Pocket] Pocket004
  BaseFeature = -> Pocket002
  Length = 5
  Length2 = 100
  Placement = pos=(0,0,0) rot=(1,0,0;1.5708rad)
  Profile = -> Sketch005
  Type = 1
FEATURE [Sketcher::SketchObject] Sketch006
  FullyConstrained = true
  MapMode = 5
  Placement = pos=(0,0,0) rot=(1,0,0;1.5708rad)
  Support = -> [DatumPlane]
  expr: Constraints[11] = <<Attributes>>.Bottom_Space_Height
  expr: Constraints[10] = <<Attributes>>.Bottom_Height_BH
  expr: Constraints[9] = <<Attributes>>.DrawerWidth_DW
  sketch-geometry (4):
    g0: LineSegment StartX=0 StartY=24 StartZ=0 EndX=410.8 EndY=24 EndZ=0
    g1: LineSegment StartX=410.8 StartY=24 StartZ=0 EndX=410.8 EndY=20 EndZ=0
    g2: LineSegment StartX=410.8 StartY=20 StartZ=0 EndX=0 EndY=20 EndZ=0
    g3: LineSegment StartX=0 StartY=20 StartZ=0 EndX=0 EndY=24 EndZ=0
  constraints (12):
    c: Coincident(g0,g1)
    c: Coincident(g1,g2)
    c: Coincident(g2,g3)
    c: Coincident(g3,g0)
    c: Horizontal(g0)
    c: Horizontal(g2)
    c: Vertical(g1)
    c: Vertical(g3)
    c: PointOnObject(g2,g-2)
    c: DistanceX(g-1,g1) = 410.8
    c: DistanceY(g2,g0) = 4
    c: DistanceY(g-1,g2) = 20
FEATURE [PartDesign::Pocket] Pocket005
  BaseFeature = -> Pocket004
  Length = 7.5
  Length2 = 100
  Placement = pos=(0,0,0) rot=(1,0,0;1.5708rad)
  Profile = -> Sketch006
  Reversed = true
  Type = 0
  expr: Length = <<Attributes>>.WallThickness_WT / 2
FEATURE [Sketcher::SketchObject] Sketch007
  FullyConstrained = true
  MapMode = 5
  Placement = pos=(0,0,0) rot=(1,0,0;1.5708rad)
  Support = -> [DatumPlane]
  expr: Constraints[50] = <<Attributes>>.DrawerWidth_DW - <<Attributes>>.WallThickness_WT * 1.5
  expr: Constraints[48] = <<Attributes>>.WallThickness_WT / 2
  expr: Constraints[22] = <<Attributes>>.ScrewPreWhole / 2
  expr: Constraints[51] = <<Attributes>>.DrawerWidth_DW - <<Attributes>>.WallThickness_WT / 2
  expr: Constraints[21] = <<Attributes>>.DrawerHeight_DH - <<Attributes>>.WallThickness_WT / 2
  expr: Constraints[49] = <<Attributes>>.WallThickness_WT * 1.5
  expr: Constraints[20] = <<Attributes>>.Bottom_Space_Height / 2
  expr: Constraints[19] = <<Attributes>>.DrawerHeight_DH - <<Attributes>>.WallThickness_WT - <<Attributes>>.Bottom_Space_Height - <<Attributes>>.Bottom_Height_BH
  expr: Constraints[64] = <<Attributes>>.SideLengt / 2
  expr: Constraints[76] = <<Attributes>>.DrawerWidth_DW + <<Attributes>>.SideLengt / 2
  sketch-geometry (30):
    g0: Circle CenterX=7.5 CenterY=56.5 CenterZ=0 NormalX=0 NormalY=0 NormalZ=1 AngleXU=0 Radius=1.5
    g1: Circle CenterX=7.5 CenterY=31.5 CenterZ=0 NormalX=0 NormalY=0 NormalZ=1 AngleXU=0 Radius=1.5
    g2: Circle CenterX=7.5 CenterY=10 CenterZ=0 NormalX=0 NormalY=0 NormalZ=1 AngleXU=0 Radius=1.5
    g3: LineSegment StartX=7.5 StartY=10 StartZ=0 EndX=7.5 EndY=31.5 EndZ=0
    g4: LineSegment StartX=7.5 StartY=31.5 StartZ=0 EndX=7.5 EndY=56.5 EndZ=0
    g5: Circle CenterX=22.5 CenterY=56.5 CenterZ=0 NormalX=0 NormalY=0 NormalZ=1 AngleXU=0 Radius=1.5
    g6: Circle CenterX=22.5 CenterY=31.5 CenterZ=0 NormalX=0 NormalY=0 NormalZ=1 AngleXU=0 Radius=1.5
    g7: Circle CenterX=22.5 CenterY=10 CenterZ=0 NormalX=0 NormalY=0 NormalZ=1 AngleXU=0 Radius=1.5
    g8: LineSegment StartX=22.5 StartY=10 StartZ=0 EndX=22.5 EndY=31.5 EndZ=0
    g9: LineSegment StartX=22.5 StartY=31.5 StartZ=0 EndX=22.5 EndY=56.5 EndZ=0
    g10: Circle CenterX=388.3 CenterY=56.5 CenterZ=0 NormalX=0 NormalY=0 NormalZ=1 AngleXU=0 Radius=1.5
    g11: Circle CenterX=388.3 CenterY=31.5 CenterZ=0 NormalX=0 NormalY=0 NormalZ=1 AngleXU=0 Radius=1.5
    g12: Circle CenterX=388.3 CenterY=10 CenterZ=0 NormalX=0 NormalY=0 NormalZ=1 AngleXU=0 Radius=1.5
    g13: LineSegment StartX=388.3 StartY=10 StartZ=0 EndX=388.3 EndY=31.5 EndZ=0
    g14: LineSegment StartX=388.3 StartY=31.5 StartZ=0 EndX=388.3 EndY=56.5 EndZ=0
    g15: Circle CenterX=403.3 CenterY=56.5 CenterZ=0 NormalX=0 NormalY=0 NormalZ=1 AngleXU=0 Radius=1.5
    g16: Circle CenterX=403.3 CenterY=31.5 CenterZ=0 NormalX=0 NormalY=0 NormalZ=1 AngleXU=0 Radius=1.5
    g17: Circle CenterX=403.3 CenterY=10 CenterZ=0 NormalX=0 NormalY=0 NormalZ=1 AngleXU=0 Radius=1.5
    g18: LineSegment StartX=403.3 StartY=10 StartZ=0 EndX=403.3 EndY=31.5 EndZ=0
    g19: LineSegment StartX=403.3 StartY=31.5 StartZ=0 EndX=403.3 EndY=56.5 EndZ=0
    g20: Circle CenterX=-10 CenterY=56.5 CenterZ=0 NormalX=0 NormalY=0 NormalZ=1 AngleXU=0 Radius=1.5
    g21: Circle CenterX=-10 CenterY=31.5 CenterZ=0 NormalX=0 NormalY=0 NormalZ=1 AngleXU=0 Radius=1.5
    g22: Circle CenterX=-10 CenterY=10 CenterZ=0 NormalX=0 NormalY=0 NormalZ=1 AngleXU=0 Radius=1.5
    g23: LineSegment StartX=-10 StartY=10 StartZ=0 EndX=-10 EndY=31.5 EndZ=0
    g24: LineSegment StartX=-10 StartY=31.5 StartZ=0 EndX=-10 EndY=56.5 EndZ=0
    g25: Circle CenterX=420.8 CenterY=56.5 CenterZ=0 NormalX=0 NormalY=0 NormalZ=1 AngleXU=0 Radius=1.5
    g26: Circle CenterX=420.8 CenterY=31.5 CenterZ=0 NormalX=0 NormalY=0 NormalZ=1 AngleXU=0 Radius=1.5
    g27: Circle CenterX=420.8 CenterY=10 CenterZ=0 NormalX=0 NormalY=0 NormalZ=1 AngleXU=0 Radius=1.5
    g28: LineSegment StartX=420.8 StartY=10 StartZ=0 EndX=420.8 EndY=31.5 EndZ=0
    g29: LineSegment StartX=420.8 StartY=31.5 StartZ=0 EndX=420.8 EndY=56.5 EndZ=0
  constraints (78):
    c: Coincident(g3,g2)
    c: Coincident(g3,g4)
    c: Vertical(g4)
    c: Vertical(g3)
    c: Coincident(g0,g4)
    c: Coincident(g1,g3)
    c: Equal(g0,g1)
    c: Equal(g1,g2)
    c: Coincident(g8,g7)
    c: Coincident(g8,g9)
    c: Vertical(g9)
    c: Vertical(g8)
    c: Coincident(g5,g9)
    c: Coincident(g6,g8)
    c: Equal(g5,g6)
    c: Equal(g6,g7)
    c: Equal(g9,g4)
    c: Equal(g3,g8)
    c: Horizontal(g2,g7)
    c: Distance(g4) = 25
    c: DistanceY(g-1,g2) = 10
    c: DistanceY(g-1,g0) = 56.5
    c: Radius(g0) = 1.5
    c: Equal(g0,g5)
    c: Coincident(g13,g12)
    c: Coincident(g13,g14)
    c: Vertical(g14)
    c: Vertical(g13)
    c: Coincident(g10,g14)
    c: Coincident(g11,g13)
    c: Equal(g10,g11)
    c: Equal(g11,g12)
    c: Coincident(g18,g17)
    c: Coincident(g18,g19)
    c: Vertical(g19)
    c: Vertical(g18)
    c: Coincident(g15,g19)
    c: Coincident(g16,g18)
    c: Equal(g15,g16)
    c: Equal(g16,g17)
    c: Equal(g10,g15)
    c: Equal(g15,g5)
    c: Equal(g9,g14)
    c: Equal(g14,g19)
    c: Equal(g8,g13)
    c: Equal(g13,g18)
    c: Horizontal(g7,g12)
    c: Horizontal(g12,g17)
    c: DistanceX(g-1,g2) = 7.5
    c: DistanceX(g-1,g7) = 22.5
    c: DistanceX(g-1,g12) = 388.3
    c: DistanceX(g-1,g17) = 403.3
    c: Coincident(g23,g22)
    c: Coincident(g23,g24)
    c: Vertical(g24)
    c: Vertical(g23)
    c: Coincident(g20,g24)
    c: Coincident(g21,g23)
    c: Equal(g20,g21)
    c: Equal(g21,g22)
    c: Horizontal(g20,g0)
    c: Equal(g22,g0)
    c: Equal(g23,g3)
    c: Equal(g24,g4)
    c: DistanceX(g22,g-1) = 10
    c: Coincident(g28,g27)
    c: Coincident(g28,g29)
    c: Vertical(g29)
    c: Vertical(g28)
    c: Coincident(g25,g29)
    c: Coincident(g26,g28)
    c: Equal(g25,g26)
    c: Equal(g26,g27)
    c: Horizontal(g27,g17)
    c: Equal(g18,g28)
    c: Equal(g19,g29)
    c: DistanceX(g-1,g27) = 420.8
    c: Equal(g27,g17)
FEATURE [PartDesign::Pocket] Pocket006
  BaseFeature = -> Pocket005
  Length = 5
  Length2 = 100
  Placement = pos=(0,0,0) rot=(1,0,0;1.5708rad)
  Profile = -> Sketch007
  Reversed = true
  Type = 1
FEATURE [Sketcher::SketchObject] Sketch008
  FullyConstrained = true
  MapMode = 5
  Placement = pos=(0,-15,3.3e-15) rot=(1,0,0;1.5708rad)
  Support = -> [DatumPlane001]
  expr: Constraints[4] = <<Attributes>>.LogicSpaceCornerRadius * 2
  expr: Constraints[29] = <<Attributes>>.LogicSpaceCornerRadius
  expr: Constraints[26] = <<Attributes>>.DrawerHeight_DH - <<Attributes>>.WallThickness_WT / 2
  expr: Constraints[31] = <<Attributes>>.LogicSpaceWidth - <<Attributes>>.LogicSpaceCornerRadius
  expr: Constraints[25] = <<Attributes>>.DrawerWidth_DW
  expr: Constraints[23] = <<Attributes>>.DrawerHeight_DH - <<Attributes>>.WallThickness_WT / 2 - (<<Attributes>>.DrawerHeight_DH - <<Attributes>>.WallThickness_WT - <<Attributes>>.Bottom_Space_Height - <<Attributes>>.Bottom_Height_BH) / 2
  expr: Constraints[24] = <<Attributes>>.WallThickness_WT * 2
  expr: Constraints[15] = <<Attributes>>.CableChannelHight
  expr: Constraints[53] = <<Attributes>>.Bottom_Space_Height + <<Attributes>>.Bottom_Height_BH * 2
  sketch-geometry (31):
    g0: LineSegment StartX=378.8 StartY=56.5 StartZ=0 EndX=280.8 EndY=56.5 EndZ=0
    g1: LineSegment StartX=280.8 StartY=27 StartZ=0 EndX=378.8 EndY=27 EndZ=0
    g2: LineSegment StartX=380.8 StartY=36.5 StartZ=0 EndX=409.8 EndY=36.5 EndZ=0
    g3: LineSegment StartX=409.8 StartY=51.5 StartZ=0 EndX=380.8 EndY=51.5 EndZ=0
    g4: ArcOfCircle CenterX=409.8 CenterY=50.5 CenterZ=0 NormalX=0 NormalY=0 NormalZ=1 AngleXU=0 Radius=1 StartAngle=0 EndAngle=1.5708
    g5: GeomPoint X=410.8 Y=51.5 Z=0
    g6: ArcOfCircle CenterX=409.8 CenterY=37.5 CenterZ=0 NormalX=0 NormalY=0 NormalZ=1 AngleXU=0 Radius=1 StartAngle=4.71239 EndAngle=6.28319
    g7: GeomPoint X=410.8 Y=36.5 Z=0
    g8: ArcOfCircle CenterX=280.8 CenterY=55.5 CenterZ=0 NormalX=0 NormalY=0 NormalZ=1 AngleXU=0 Radius=1 StartAngle=1.5708 EndAngle=3.14159
    g9: GeomPoint X=279.8 Y=56.5 Z=0
    g10: ArcOfCircle CenterX=280.8 CenterY=28 CenterZ=0 NormalX=0 NormalY=0 NormalZ=1 AngleXU=0 Radius=1 StartAngle=3.14159 EndAngle=4.71239
    g11: GeomPoint X=279.8 Y=27 Z=0
    g12: LineSegment StartX=410.8 StartY=37.5 StartZ=0 EndX=410.8 EndY=44 EndZ=0
    g13: LineSegment StartX=410.8 StartY=44 StartZ=0 EndX=410.8 EndY=50.5 EndZ=0
    g14: ArcOfCircle CenterX=378.8 CenterY=55.5 CenterZ=0 NormalX=0 NormalY=0 NormalZ=1 AngleXU=0 Radius=1 StartAngle=0 EndAngle=1.5708
    g15: ArcOfCircle CenterX=380.8 CenterY=52.5 CenterZ=0 NormalX=0 NormalY=0 NormalZ=1 AngleXU=0 Radius=1 StartAngle=3.14159 EndAngle=4.71239
    g16: LineSegment StartX=379.8 StartY=55.5 StartZ=0 EndX=379.8 EndY=52.5 EndZ=0
    g17: LineSegment StartX=379.8 StartY=35.5 StartZ=0 EndX=379.8 EndY=28 EndZ=0
    g18: ArcOfCircle CenterX=380.8 CenterY=35.5 CenterZ=0 NormalX=0 NormalY=0 NormalZ=1 AngleXU=0 Radius=1 StartAngle=1.5708 EndAngle=3.14159
    g19: GeomPoint X=379.8 Y=36.5 Z=0
    g20: ArcOfCircle CenterX=378.8 CenterY=28 CenterZ=0 NormalX=0 NormalY=0 NormalZ=1 AngleXU=0 Radius=1 StartAngle=4.71239 EndAngle=6.28319
    g21: GeomPoint X=379.8 Y=27 Z=0
    g22: LineSegment StartX=279.8 StartY=55.5 StartZ=0 EndX=279.8 EndY=52.5 EndZ=0
    g23: LineSegment StartX=278.8 StartY=51.5 StartZ=0 EndX=1 EndY=51.5 EndZ=0
    g24: LineSegment StartX=0 StartY=50.5 StartZ=0 EndX=0 EndY=37.5 EndZ=0
    g25: LineSegment StartX=1 StartY=36.5 StartZ=0 EndX=278.8 EndY=36.5 EndZ=0
    g26: LineSegment StartX=279.8 StartY=35.5 StartZ=0 EndX=279.8 EndY=28 EndZ=0
    g27: ArcOfCircle CenterX=278.8 CenterY=52.5 CenterZ=0 NormalX=0 NormalY=0 NormalZ=1 AngleXU=0 Radius=1 StartAngle=4.71239 EndAngle=6.28319
    g28: ArcOfCircle CenterX=1 CenterY=50.5 CenterZ=0 NormalX=0 NormalY=0 NormalZ=1 AngleXU=0 Radius=1 StartAngle=1.5708 EndAngle=3.14159
    g29: ArcOfCircle CenterX=1 CenterY=37.5 CenterZ=0 NormalX=0 NormalY=0 NormalZ=1 AngleXU=0 Radius=1 StartAngle=3.14159 EndAngle=4.71239
    g30: ArcOfCircle CenterX=278.8 CenterY=35.5 CenterZ=0 NormalX=0 NormalY=0 NormalZ=1 AngleXU=0 Radius=1 StartAngle=-9e-16 EndAngle=1.5708
  constraints (81):
    c: Horizontal(g0)
    c: Horizontal(g1)
    c: Horizontal(g2)
    c: Horizontal(g3)
    c: DistanceX(g0,g3) = 2
    c: PointOnObject(g5,g3)
    c: Tangent(g3,g4) = -1.5708
    c: PointOnObject(g7,g2)
    c: Tangent(g2,g6) = -1.5708
    c: PointOnObject(g9,g0)
    c: Tangent(g0,g8) = -1.5708
    c: PointOnObject(g11,g1)
    c: Tangent(g1,g10) = -1.5708
    c: Equal(g10,g8)
    c: Equal(g6,g4)
    c: DistanceY(g2,g3) = 15
    c: Tangent(g6,g12) = -1.5708
    c: Coincident(g12,g13)
    c: Coincident(g13,g4)
    c: Vertical(g13)
    c: Equal(g12,g13)
    c: Vertical(g12)
    c: Horizontal(g4,g4)
    c: DistanceY(g-1,g12) = 44
    c: DistanceX(g3,g4) = 30
    c: DistanceX(g-1,g12) = 410.8
    c: DistanceY(g-1,g0) = 56.5
    c: Vertical(g6,g7)
    c: Vertical(g5,g4)
    c: Radius(g6) = 1
    c: Equal(g8,g4)
    c: DistanceX(g9,g0) = 99
    c: Coincident(g14,g0)
    c: Horizontal(g14,g14)
    c: Angle(g14) = 1.5708
    c: Equal(g14,g8)
    c: Coincident(g15,g3)
    c: Equal(g15,g14)
    c: Horizontal(g15,g15)
    c: Angle(g15) = 1.5708
    c: Coincident(g16,g14)
    c: Coincident(g16,g15)
    c: Vertical(g17)
    c: PointOnObject(g19,g2)
    c: PointOnObject(g19,g17)
    c: Tangent(g2,g18) = 1.5708
    c: Tangent(g17,g18) = -1.5708
    c: PointOnObject(g21,g1)
    c: PointOnObject(g21,g17)
    c: Tangent(g1,g20) = -1.5708
    c: Tangent(g17,g20) = 1.5708
    c: Equal(g20,g18)
    c: Equal(g18,g15)
    c: DistanceY(g-1,g10) = 28
    c: Vertical(g2,g3)
    c: Tangent(g8,g22) = -1.5708
    c: Horizontal(g23)
    c: Vertical(g24)
    c: Horizontal(g25)
    c: Coincident(g26,g10)
    c: Vertical(g26)
    c: Tangent(g22,g27) = 1.5708
    c: Tangent(g23,g27) = 1.5708
    c: Tangent(g23,g28) = -1.5708
    c: Tangent(g24,g28) = -1.5708
    c: Tangent(g24,g29) = -1.5708
    c: Tangent(g25,g29) = -1.5708
    c: Tangent(g25,g30) = 1.5708
    c: Tangent(g26,g30) = 1.5708
    c: Equal(g30,g29)
    c: Equal(g29,g28)
    c: Equal(g28,g27)
    c: Equal(g27,g8)
    c: Horizontal(g27,g15)
    c: Vertical(g22)
    c: Vertical(g9,g8)
    c: Horizontal(g30,g18)
    c: Vertical(g27,g30)
    c: Vertical(g11,g10)
    c: Horizontal(g10,g10)
    c: PointOnObject(g24,g-2)
FEATURE [PartDesign::Pocket] Pocket007
  BaseFeature = -> Pocket006
  Length = 7.5
  Length2 = 100
  Placement = pos=(0,0,0) rot=(1,0,0;1.5708rad)
  Profile = -> Sketch008
  Type = 0
  expr: Length = <<Attributes>>.WallThickness_WT / 2
FEATURE [Sketcher::SketchObject] Sketch010
  FullyConstrained = true
  MapMode = 5
  Placement = pos=(0,0,0) rot=(1,0,0;1.5708rad)
  Support = -> [DatumPlane]
  expr: Constraints[26] = <<Attributes>>.LogicSpaceCornerRadius
  expr: Constraints[29] = <<Attributes>>.DrawerHeight_DH - <<Attributes>>.WallThickness_WT / 2
  expr: Constraints[32] = <<Attributes>>.LogicBoardStandoffHoleSideSpace + <<Attributes>>.LogicBoardStandoffHoleDiameter / 2
  expr: Constraints[38] = <<Attributes>>.LogicBoardStandoffHoleSideSpace + <<Attributes>>.LogicBoardStandoffHoleDiameter / 2
  expr: Constraints[27] = <<Attributes>>.LogicSpaceWidth
  expr: Constraints[30] = <<Attributes>>.LogicBoardScrewHeadDiameter / 2
  expr: Constraints[28] = <<Attributes>>.WallThickness_WT / 2
  expr: Constraints[31] = <<Attributes>>.DrawerWidth_DW - <<Attributes>>.WallThickness_WT * 2 - <<Attributes>>.LogicSpaceCornerRadius
  expr: Constraints[33] = <<Attributes>>.LogicBoardStandoffHoleSideSpace + <<Attributes>>.LogicBoardStandoffHoleDiameter / 2
  expr: Constraints[34] = <<Attributes>>.LogicBoardStandoffHoleSideSpace + <<Attributes>>.LogicBoardStandoffHoleDiameter / 2
  expr: Constraints[36] = <<Attributes>>.LogicBoardStandoffHoleSideSpace + <<Attributes>>.LogicBoardStandoffHoleDiameter / 2
  expr: Constraints[35] = <<Attributes>>.LogicBoardStandoffHoleSideSpace + <<Attributes>>.LogicBoardStandoffHoleDiameter / 2
  expr: Constraints[37] = <<Attributes>>.LogicBoardStandoffHoleSideSpace + <<Attributes>>.LogicBoardStandoffHoleDiameter / 2
  expr: Constraints[39] = <<Attributes>>.LogicBoardStandoffHoleSideSpace + <<Attributes>>.LogicBoardStandoffHoleDiameter / 2
  sketch-geometry (16):
    g0: Circle CenterX=287.3 CenterY=49 CenterZ=0 NormalX=0 NormalY=0 NormalZ=1 AngleXU=0 Radius=3
    g1: Circle CenterX=372.3 CenterY=49 CenterZ=0 NormalX=0 NormalY=0 NormalZ=1 AngleXU=0 Radius=3
    g2: Circle CenterX=287.3 CenterY=15 CenterZ=0 NormalX=0 NormalY=0 NormalZ=1 AngleXU=0 Radius=3
    g3: Circle CenterX=372.3 CenterY=15 CenterZ=0 NormalX=0 NormalY=0 NormalZ=1 AngleXU=0 Radius=3
    g4: LineSegment StartX=280.8 StartY=56.5 StartZ=0 EndX=378.8 EndY=56.5 EndZ=0
    g5: LineSegment StartX=379.8 StartY=55.5 StartZ=0 EndX=379.8 EndY=8.5 EndZ=0
    g6: LineSegment StartX=378.8 StartY=7.5 StartZ=0 EndX=280.8 EndY=7.5 EndZ=0
    g7: LineSegment StartX=279.8 StartY=8.5 StartZ=0 EndX=279.8 EndY=55.5 EndZ=0
    g8: ArcOfCircle CenterX=280.8 CenterY=55.5 CenterZ=0 NormalX=0 NormalY=0 NormalZ=1 AngleXU=0 Radius=1 StartAngle=1.5708 EndAngle=3.14159
    g9: GeomPoint X=279.8 Y=56.5 Z=0
    g10: ArcOfCircle CenterX=280.8 CenterY=8.5 CenterZ=0 NormalX=0 NormalY=0 NormalZ=1 AngleXU=0 Radius=1 StartAngle=3.14159 EndAngle=4.71239
    g11: GeomPoint X=279.8 Y=7.5 Z=0
    g12: ArcOfCircle CenterX=378.8 CenterY=8.5 CenterZ=0 NormalX=0 NormalY=0 NormalZ=1 AngleXU=0 Radius=1 StartAngle=4.71239 EndAngle=6.28319
    g13: GeomPoint X=379.8 Y=7.5 Z=0
    g14: ArcOfCircle CenterX=378.8 CenterY=55.5 CenterZ=0 NormalX=0 NormalY=0 NormalZ=1 AngleXU=0 Radius=1 StartAngle=3.9e-15 EndAngle=1.5708
    g15: GeomPoint X=379.8 Y=56.5 Z=0
  constraints (40):
    c: Horizontal(g4)
    c: Horizontal(g6)
    c: Vertical(g5)
    c: Vertical(g7)
    c: Equal(g0,g1)
    c: Equal(g1,g2)
    c: Equal(g2,g3)
    c: PointOnObject(g9,g4)
    c: PointOnObject(g9,g7)
    c: Tangent(g4,g8) = 1.5708
    c: Tangent(g7,g8) = 1.5708
    c: PointOnObject(g11,g6)
    c: PointOnObject(g11,g7)
    c: Tangent(g6,g10) = 1.5708
    c: Tangent(g7,g10) = 1.5708
    c: PointOnObject(g13,g5)
    c: PointOnObject(g13,g6)
    c: Tangent(g5,g12) = 1.5708
    c: Tangent(g6,g12) = 1.5708
    c: PointOnObject(g15,g4)
    c: PointOnObject(g15,g5)
    c: Tangent(g4,g14) = 1.5708
    c: Tangent(g5,g14) = 1.5708
    c: Equal(g8,g10)
    c: Equal(g10,g12)
    c: Equal(g12,g14)
    c: Radius(g8) = 1
    c: DistanceX(g9,g15) = 100
    c: DistanceY(g-1,g11) = 7.5
    c: DistanceY(g-1,g9) = 56.5
    c: Radius(g0) = 3
    c: DistanceX(g-1,g15) = 379.8
    c: DistanceY(g1,g4) = 7.5
    c: DistanceX(g1,g5) = 7.5
    c: DistanceX(g7,g0) = 7.5
    c: DistanceY(g0,g4) = 7.5
    c: DistanceX(g7,g2) = 7.5
    c: DistanceY(g6,g2) = 7.5
    c: DistanceX(g3,g5) = 7.5
    c: DistanceY(g6,g3) = 7.5
FEATURE [PartDesign::Pocket] Pocket009
  BaseFeature = -> Pocket007
  Length = 3
  Length2 = 100
  Placement = pos=(0,0,0) rot=(1,0,0;1.5708rad)
  Profile = -> Sketch010
  Reversed = true
  Type = 0
  expr: Length = <<Attributes>>.LogicBoardScrewHeadHeight
FEATURE [PartDesign::Body] InnerFrontWall001
  Group = -> [LCS_0001,Sketch,Pad,Sketch001,Pocket,Sketch002,Pocket001,Sketch003,Pocket002,Sketch005,Pocket004,DatumPlane,DatumPlane001,Sketch006,Pocket005,Sketch007,Pocket006,Sketch008,Pocket007,Sketch010,Pocket009]
  Origin = -> Origin001
  Tip = -> Pocket009
FEATURE [PartDesign::CoordinateSystem] InnerFrontWall_InnerRightWall_  label="InnerFrontWall-InnerRightWall "
  AttacherType = Attacher::AttachEngine3D
  AttachmentOffset = pos=(380.8,-7.5,0) rot=(0,0,1;0rad)
  MapMode = 2
  Placement = pos=(380.8,-7.5,0) rot=(0,0,1;0rad)
  Support = -> [LCS_0]
  expr: .AttachmentOffset.Base.x = <<Attributes>>.DrawerWidth_DW - <<Attributes>>.WallThickness_WT * 2
  expr: .AttachmentOffset.Base.y = <<Attributes>>.WallThickness_WT / -2
FEATURE [PartDesign::CoordinateSystem] InnerFrontWall_OuterRightWall  label="InnerFrontWall-OuterRightWall"
  AttacherType = Attacher::AttachEngine3D
  AttachmentOffset = pos=(395.8,-7.5,0) rot=(0,0,1;0rad)
  MapMode = 2
  Placement = pos=(395.8,-7.5,0) rot=(0,0,1;0rad)
  Support = -> [LCS_0]
  expr: .AttachmentOffset.Base.x = <<Attributes>>.DrawerWidth_DW - <<Attributes>>.WallThickness_WT
  expr: .AttachmentOffset.Base.y = <<Attributes>>.WallThickness_WT / -2
FEATURE [PartDesign::CoordinateSystem] InnerFrontWall_Bottom  label="InnerFrontWall-Bottom"
  AttacherType = Attacher::AttachEngine3D
  AttachmentOffset = pos=(22.5,-7.5,20) rot=(0,0,1;0rad)
  MapMode = 2
  Placement = pos=(22.5,-7.5,20) rot=(0,0,1;0rad)
  Support = -> [LCS_0]
  expr: .AttachmentOffset.Base.x = <<Attributes>>.WallThickness_WT * 1.5
  expr: .AttachmentOffset.Base.y = <<Attributes>>.WallThickness_WT / -2
  expr: .AttachmentOffset.Base.z = <<Attributes>>.Bottom_Space_Height
FEATURE [PartDesign::CoordinateSystem] S1
  AttacherType = Attacher::AttachEngine3D
  MapMode = 11
  Placement = pos=(287.3,-3,49) rot=(0.57735,-0.57735,-0.57735;4.18879rad)
  Support = -> [Pocket009]
FEATURE [PartDesign::CoordinateSystem] S2
  AttacherType = Attacher::AttachEngine3D
  MapMode = 11
  Placement = pos=(287.3,-3,15) rot=(0.57735,-0.57735,-0.57735;4.18879rad)
  Support = -> [Pocket009]
FEATURE [PartDesign::CoordinateSystem] S3
  AttacherType = Attacher::AttachEngine3D
  MapMode = 11
  Placement = pos=(372.3,-3,15) rot=(0.57735,-0.57735,-0.57735;4.18879rad)
  Support = -> [Pocket009]
FEATURE [PartDesign::CoordinateSystem] S4
  AttacherType = Attacher::AttachEngine3D
  MapMode = 11
  Placement = pos=(372.3,-3,49) rot=(0.57735,-0.57735,-0.57735;4.18879rad)
  Support = -> [Pocket009]
FEATURE [PartDesign::CoordinateSystem] InnerFrontWall_OuterFrontWall  label="InnerFrontWall-OuterFrontWall"
  AttacherType = Attacher::AttachEngine3D
  MapMode = 1
  Placement = pos=(-20,-15,8.3e-15) rot=(0,0,1;0rad)
  Support = -> [Pocket009]
FEATURE [App::Part] InnerFrontWall
  Group = -> [LCS_0,InnerFrontWall001,PropertyBag,InnerFrontWall_InnerRightWall_,InnerFrontWall_OuterRightWall,InnerFrontWall_Bottom,S1,S2,S3,S4,InnerFrontWall_OuterFrontWall]
  Origin = -> Origin
---- part InnerRightWall.FCStd = doc fcstd_30c90f9726dd ----
FCSTD DOCUMENT  (FreeCAD 0.19R24291 (Git))
Label: InnerRightWall
License: All rights reserved
LicenseURL: http://en.wikipedia.org/wiki/All_rights_reserved
objects: Sketcher::SketchObject×7, PartDesign::Pocket×6, PartDesign::CoordinateSystem×2, PartDesign::LinearPattern×2, PartDesign::MultiTransform×2, App::FeaturePython×1, PartDesign::Pad×1, PartDesign::Body×1, App::Part×1
note: 28 computed .brp shape members not serialized (recipe doc carries the construction recipe); baked Part::Feature solids carry a one-line shape summary decoded from their .brp

FEATURE [PartDesign::CoordinateSystem] LCS_0
  AttacherType = Attacher::AttachEngine3D
  MapMode = 2
  Support = -> [X_Axis]
FEATURE [PartDesign::CoordinateSystem] LCS_0001
  AttacherType = Attacher::AttachEngine3D
  MapMode = 2
  Support = -> [X_Axis001]
FEATURE [Sketcher::SketchObject] Sketch
  FullyConstrained = true
  MapMode = 5
  Placement = pos=(0,0,0) rot=(0.57735,0.57735,0.57735;2.0944rad)
  Support = -> [YZ_Plane001]
  expr: Constraints[7] = <<Attributes>>.InnerWallDepth
  expr: Constraints[8] = <<Attributes>>.DrawerHeight_DH
  sketch-geometry (4):
    g0: LineSegment StartX=358.3 StartY=0 StartZ=0 EndX=0 EndY=0 EndZ=0
    g1: LineSegment StartX=0 StartY=0 StartZ=0 EndX=0 EndY=64 EndZ=0
    g2: LineSegment StartX=0 StartY=64 StartZ=0 EndX=358.3 EndY=64 EndZ=0
    g3: LineSegment StartX=358.3 StartY=64 StartZ=0 EndX=358.3 EndY=0 EndZ=0
  constraints (11):
    c: Coincident(g0,g1)
    c: Coincident(g1,g2)
    c: Coincident(g2,g3)
    c: Horizontal(g0)
    c: Horizontal(g2)
    c: Vertical(g1)
    c: Vertical(g3)
    c: Distance(g2) = 358.3
    c: Distance(g3) = 64
    c: Coincident(g3,g0)
    c: Coincident(g-1,g0)
FEATURE [App::FeaturePython] PropertyBag  label="Attributes"  # WARN: FeaturePython — macro-defined, semantics opaque (R4)
  BackWidth = 395.8
  Back_Space = 100
  BottomDepth = 365.8
  BottomWidth = 365.8
  Bottom_Height_BH = 4
  Bottom_Space_Height = 20
  Box_Tolerance = 0.2
  Boxes_Depth = 5
  Boxes_Height = 40
  Boxes_Width = 5
  CableChannelHight = 15
  CableChannelRadius = 2
  CustomPropertyGroups = shape | attributes
  DrawerDepth_DD = 465.8
  DrawerHeight_DH = 64
  DrawerWidth_DW = 410.8
  InnerWallDepth = 358.3
  ScrewPreWhole = 3
  ScrewPreWholeDepth = 20
  WallThickness_WT = 15
  expr: BottomDepth = Boxes_Depth * 70mm + WallThickness_WT + Box_Tolerance * (Boxes_Width - 1)
  expr: DrawerHeight_DH = Boxes_Height + Bottom_Height_BH + Bottom_Space_Height
  expr: BackWidth = DrawerWidth_DW - WallThickness_WT
  expr: DrawerWidth_DW = Boxes_Width * 70mm + WallThickness_WT * 4 + Box_Tolerance * (Boxes_Width - 1)
  expr: BottomWidth = Boxes_Width * 70mm + WallThickness_WT + Box_Tolerance * (Boxes_Width - 1)
  expr: DrawerDepth_DD = Boxes_Depth * 70mm + WallThickness_WT + Back_Space + Box_Tolerance * (Boxes_Width - 1)
  expr: InnerWallDepth = Boxes_Depth * 70mm + WallThickness_WT * 0.5 + Box_Tolerance * (Boxes_Width - 1)
FEATURE [PartDesign::Pad] Pad
  Direction = (1,1,1)
  Length = 15
  Length2 = 100
  Placement = pos=(0,0,0) rot=(0.57735,0.57735,0.57735;2.0944rad)
  Profile = -> Sketch
  Type = 0
  expr: Length = <<Attributes>>.WallThickness_WT
FEATURE [Sketcher::SketchObject] Sketch001
  FullyConstrained = true
  MapMode = 5
  Placement = pos=(3e-16,0,0) rot=(0.57735,0.57735,-0.57735;4.18879rad)
  Support = -> [Pad]
  expr: Constraints[9] = <<Attributes>>.Bottom_Space_Height
  expr: Constraints[10] = <<Attributes>>.Bottom_Height_BH
  expr: Constraints[11] = <<Attributes>>.InnerWallDepth
  sketch-geometry (4):
    g0: LineSegment StartX=0 StartY=-20 StartZ=0 EndX=358.3 EndY=-20 EndZ=0
    g1: LineSegment StartX=358.3 StartY=-20 StartZ=0 EndX=358.3 EndY=-24 EndZ=0
    g2: LineSegment StartX=358.3 StartY=-24 StartZ=0 EndX=0 EndY=-24 EndZ=0
    g3: LineSegment StartX=0 StartY=-24 StartZ=0 EndX=0 EndY=-20 EndZ=0
  constraints (12):
    c: Coincident(g0,g1)
    c: Coincident(g1,g2)
    c: Coincident(g2,g3)
    c: Coincident(g3,g0)
    c: Horizontal(g0)
    c: Horizontal(g2)
    c: Vertical(g1)
    c: Vertical(g3)
    c: PointOnObject(g0,g-2)
    c: DistanceY(g0,g-1) = 20
    c: Distance(g3) = 4
    c: Distance(g2) = 358.3
FEATURE [PartDesign::Pocket] Pocket
  BaseFeature = -> Pad
  Length = 7.5
  Length2 = 100
  Placement = pos=(0,0,0) rot=(0.57735,0.57735,0.57735;2.0944rad)
  Profile = -> Sketch001
  Type = 0
  expr: Length = <<Attributes>>.WallThickness_WT / 2
FEATURE [Sketcher::SketchObject] Sketch002
  FullyConstrained = true
  MapMode = 5
  Placement = pos=(0,0,0) rot=(-0.57735,-0.57735,0.57735;4.18879rad)
  Support = -> [Pocket]
  expr: Constraints[3] = <<Attributes>>.WallThickness_WT / 2
  expr: Constraints[4] = <<Attributes>>.Bottom_Space_Height / 2
  expr: Constraints[5] = <<Attributes>>.DrawerHeight_DH - <<Attributes>>.WallThickness_WT / 2
  expr: Constraints[6] = <<Attributes>>.DrawerHeight_DH - <<Attributes>>.WallThickness_WT - <<Attributes>>.Bottom_Space_Height - <<Attributes>>.Bottom_Height_BH
  expr: Constraints[12] = <<Attributes>>.ScrewPreWhole / 2
  sketch-geometry (5):
    g0: LineSegment StartX=-56.5 StartY=7.5 StartZ=0 EndX=-31.5 EndY=7.5 EndZ=0
    g1: LineSegment StartX=-31.5 StartY=7.5 StartZ=0 EndX=-10 EndY=7.5 EndZ=0
    g2: Circle CenterX=-56.5 CenterY=7.5 CenterZ=0 NormalX=0 NormalY=0 NormalZ=1 AngleXU=0 Radius=1.5
    g3: Circle CenterX=-31.5 CenterY=7.5 CenterZ=0 NormalX=0 NormalY=0 NormalZ=1 AngleXU=0 Radius=1.5
    g4: Circle CenterX=-10 CenterY=7.5 CenterZ=0 NormalX=0 NormalY=0 NormalZ=1 AngleXU=0 Radius=1.5
  constraints (13):
    c: Horizontal(g0)
    c: Coincident(g0,g1)
    c: Horizontal(g1)
    c: DistanceY(g-1,g1) = 7.5
    c: DistanceX(g1,g-1) = 10
    c: DistanceX(g0,g-1) = 56.5
    c: Distance(g0) = 25
    c: Coincident(g2,g0)
    c: Coincident(g3,g0)
    c: Coincident(g4,g1)
    c: Equal(g2,g3)
    c: Equal(g3,g4)
    c: Radius(g2) = 1.5
FEATURE [PartDesign::Pocket] Pocket001
  BaseFeature = -> Pocket
  Length = 20
  Length2 = 100
  Placement = pos=(0,0,0) rot=(0.57735,0.57735,0.57735;2.0944rad)
  Profile = -> Sketch002
  Type = 0
  expr: Length = <<Attributes>>.ScrewPreWholeDepth
FEATURE [Sketcher::SketchObject] Sketch003
  FullyConstrained = true
  MapMode = 5
  Placement = pos=(1.577e-13,358.3,-7.88e-14) rot=(0.57735,0.57735,0.57735;4.18879rad)
  Support = -> [Pocket001]
  expr: Constraints[3] = <<Attributes>>.DrawerHeight_DH - <<Attributes>>.WallThickness_WT - <<Attributes>>.Bottom_Space_Height - <<Attributes>>.Bottom_Height_BH
  expr: Constraints[4] = <<Attributes>>.WallThickness_WT / 2
  expr: Constraints[5] = <<Attributes>>.Bottom_Space_Height / 2
  expr: Constraints[6] = <<Attributes>>.DrawerHeight_DH - <<Attributes>>.WallThickness_WT / 2
  expr: Constraints[12] = <<Attributes>>.ScrewPreWhole / 2
  sketch-geometry (5):
    g0: LineSegment StartX=10 StartY=7.5 StartZ=0 EndX=31.5 EndY=7.5 EndZ=0
    g1: LineSegment StartX=31.5 StartY=7.5 StartZ=0 EndX=56.5 EndY=7.5 EndZ=0
    g2: Circle CenterX=10 CenterY=7.5 CenterZ=0 NormalX=0 NormalY=0 NormalZ=1 AngleXU=0 Radius=1.5
    g3: Circle CenterX=31.5 CenterY=7.5 CenterZ=0 NormalX=0 NormalY=0 NormalZ=1 AngleXU=0 Radius=1.5
    g4: Circle CenterX=56.5 CenterY=7.5 CenterZ=0 NormalX=0 NormalY=0 NormalZ=1 AngleXU=0 Radius=1.5
  constraints (13):
    c: Horizontal(g0)
    c: Coincident(g0,g1)
    c: Horizontal(g1)
    c: Distance(g1) = 25
    c: DistanceY(g-1,g0) = 7.5
    c: DistanceX(g-1,g0) = 10
    c: DistanceX(g-1,g1) = 56.5
    c: Coincident(g2,g0)
    c: Coincident(g3,g0)
    c: Coincident(g4,g1)
    c: Equal(g2,g3)
    c: Equal(g3,g4)
    c: Radius(g2) = 1.5
FEATURE [PartDesign::Pocket] Pocket002
  BaseFeature = -> Pocket001
  Length = 20
  Length2 = 100
  Placement = pos=(0,0,0) rot=(0.57735,0.57735,0.57735;2.0944rad)
  Profile = -> Sketch003
  Type = 0
  expr: Length = <<Attributes>>.ScrewPreWholeDepth
FEATURE [Sketcher::SketchObject] Sketch004
  FullyConstrained = true
  MapMode = 5
  Placement = pos=(15,-3.3e-15,5e-15) rot=(0.57735,0.57735,0.57735;2.0944rad)
  Support = -> [Pocket002]
  expr: Constraints[2] = (<<Attributes>>.DrawerHeight_DH - <<Attributes>>.WallThickness_WT - <<Attributes>>.Bottom_Space_Height - <<Attributes>>.Bottom_Height_BH) / 2
  expr: Constraints[3] = <<Attributes>>.DrawerHeight_DH - <<Attributes>>.WallThickness_WT / 2
  expr: Constraints[16] = <<Attributes>>.InnerWallDepth
  expr: Constraints[17] = <<Attributes>>.CableChannelHight
  sketch-geometry (6):
    g0: LineSegment StartX=0 StartY=56.5 StartZ=0 EndX=0 EndY=44 EndZ=0
    g1: LineSegment StartX=0 StartY=36.5 StartZ=0 EndX=358.3 EndY=36.5 EndZ=0
    g2: LineSegment StartX=358.3 StartY=36.5 StartZ=0 EndX=358.3 EndY=51.5 EndZ=0
    g3: LineSegment StartX=358.3 StartY=51.5 StartZ=0 EndX=0 EndY=51.5 EndZ=0
    g4: LineSegment StartX=0 StartY=51.5 StartZ=0 EndX=0 EndY=44 EndZ=0
    g5: LineSegment StartX=0 StartY=44 StartZ=0 EndX=0 EndY=36.5 EndZ=0
  constraints (18):
    c: PointOnObject(g0,g-2)
    c: PointOnObject(g0,g-2)
    c: Distance(g0) = 12.5
    c: DistanceY(g-1,g0) = 56.5
    c: Coincident(g1,g2)
    c: Coincident(g2,g3)
    c: Horizontal(g1)
    c: Horizontal(g3)
    c: Vertical(g2)
    c: Coincident(g3,g4)
    c: Vertical(g4)
    c: Coincident(g4,g5)
    c: Coincident(g5,g1)
    c: Vertical(g5)
    c: Coincident(g4,g0)
    c: Equal(g4,g5)
    c: Distance(g3) = 358.3
    c: Distance(g2) = 15
FEATURE [PartDesign::Pocket] Pocket003
  BaseFeature = -> Pocket002
  Length = 7.5
  Length2 = 100
  Placement = pos=(0,0,0) rot=(0.57735,0.57735,0.57735;2.0944rad)
  Profile = -> Sketch004
  Type = 0
  expr: Length = <<Attributes>>.WallThickness_WT / 2
FEATURE [Sketcher::SketchObject] Sketch005
  FullyConstrained = true
  MapMode = 5
  Placement = pos=(15,-3.3e-15,6.6e-15) rot=(0.57735,0.57735,0.57735;2.0944rad)
  Support = -> [Pocket003]
  expr: Constraints[6] = (<<Attributes>>.WallThickness_WT / 2 + 70mm + <<Attributes>>.Box_Tolerance / 2) / 2 - <<Attributes>>.CableChannelHight / 2
  expr: Constraints[7] = <<Attributes>>.CableChannelHight
  expr: Constraints[22] = <<Attributes>>.DrawerHeight_DH - <<Attributes>>.WallThickness_WT / 2 - (<<Attributes>>.DrawerHeight_DH - <<Attributes>>.WallThickness_WT - <<Attributes>>.Bottom_Space_Height - <<Attributes>>.Bottom_Height_BH) / 2 - <<Attributes>>.CableChannelHight / 2
  expr: Constraints[23] = <<Attributes>>.CableChannelRadius
  sketch-geometry (8):
    g0: LineSegment StartX=46.3 StartY=34.5 StartZ=0 EndX=46.3 EndY=0 EndZ=0
    g1: LineSegment StartX=46.3 StartY=0 StartZ=0 EndX=31.3 EndY=0 EndZ=0
    g2: LineSegment StartX=31.3 StartY=0 StartZ=0 EndX=31.3 EndY=34.5 EndZ=0
    g3: ArcOfCircle CenterX=29.3 CenterY=34.5 CenterZ=0 NormalX=0 NormalY=0 NormalZ=1 AngleXU=0 Radius=2 StartAngle=0 EndAngle=1.5708
    g4: ArcOfCircle CenterX=48.3 CenterY=34.5 CenterZ=0 NormalX=0 NormalY=0 NormalZ=1 AngleXU=0 Radius=2 StartAngle=1.5708 EndAngle=3.14159
    g5: LineSegment StartX=29.3 StartY=36.5 StartZ=0 EndX=48.3 EndY=36.5 EndZ=0
    g6: LineSegment StartX=29.3 StartY=34.5 StartZ=0 EndX=31.3 EndY=34.5 EndZ=0
    g7: LineSegment StartX=46.3 StartY=34.5 StartZ=0 EndX=48.3 EndY=34.5 EndZ=0
  constraints (24):
    c: Coincident(g0,g1)
    c: Coincident(g1,g2)
    c: Horizontal(g1)
    c: Vertical(g0)
    c: Vertical(g2)
    c: PointOnObject(g1,g-1)
    c: DistanceX(g-1,g1) = 31.3
    c: Distance(g1) = 15
    c: Coincident(g3,g2)
    c: Coincident(g4,g0)
    c: Coincident(g5,g3)
    c: Coincident(g5,g4)
    c: Horizontal(g5)
    c: Equal(g4,g3)
    c: Coincident(g6,g3)
    c: Coincident(g6,g2)
    c: Coincident(g7,g0)
    c: Coincident(g7,g4)
    c: Horizontal(g7)
    c: Horizontal(g6)
    c: Angle(g3) = 1.5708
    c: Angle(g4) = 1.5708
    c: DistanceY(g1,g3) = 36.5
    c: Radius(g3) = 2
FEATURE [PartDesign::Pocket] Pocket004
  BaseFeature = -> Pocket003
  Length = 3.75
  Length2 = 100
  Placement = pos=(0,0,0) rot=(0.57735,0.57735,0.57735;2.0944rad)
  Profile = -> Sketch005
  Type = 0
  expr: Length = <<Attributes>>.WallThickness_WT / 4
FEATURE [PartDesign::LinearPattern] LinearPattern
  Direction = -> Y_Axis001
  Length = 280.8
  Occurrences = 5
  Placement = pos=(0,0,0) rot=(0.57735,0.57735,0.57735;2.0944rad)
  expr: Length = (<<Attributes>>.Boxes_Depth - 1) * (70mm + <<Attributes>>.Box_Tolerance)
  expr: Occurrences = <<Attributes>>.Boxes_Depth
FEATURE [PartDesign::MultiTransform] MultiTransform
  BaseFeature = -> Pocket004
  Originals = -> [Pocket004]
  Placement = pos=(0,0,0) rot=(0.57735,0.57735,0.57735;2.0944rad)
  Transformations = -> [LinearPattern]
FEATURE [Sketcher::SketchObject] Sketch006
  FullyConstrained = true
  MapMode = 5
  Placement = pos=(11.25,0,4.9e-15) rot=(0.57735,0.57735,0.57735;2.0944rad)
  Support = -> [MultiTransform]
  expr: Constraints[7] = (<<Attributes>>.WallThickness_WT / 2 + 70mm + <<Attributes>>.Box_Tolerance / 2) / 2 - <<Attributes>>.CableChannelHight / 2
  expr: Constraints[8] = <<Attributes>>.CableChannelHight
  expr: Constraints[9] = <<Attributes>>.Bottom_Space_Height / 3
  expr: Constraints[19] = <<Attributes>>.CableChannelRadius
  sketch-geometry (8):
    g0: LineSegment StartX=31.3 StartY=0 StartZ=0 EndX=46.3 EndY=0 EndZ=0
    g1: LineSegment StartX=46.3 StartY=0 StartZ=0 EndX=46.3 EndY=4.66667 EndZ=0
    g2: LineSegment StartX=44.3 StartY=6.66667 StartZ=0 EndX=33.3 EndY=6.66667 EndZ=0
    g3: LineSegment StartX=31.3 StartY=4.66667 StartZ=0 EndX=31.3 EndY=0 EndZ=0
    g4: ArcOfCircle CenterX=33.3 CenterY=4.66667 CenterZ=0 NormalX=0 NormalY=0 NormalZ=1 AngleXU=0 Radius=2 StartAngle=1.5708 EndAngle=3.14159
    g5: GeomPoint X=31.3 Y=6.66667 Z=0
    g6: ArcOfCircle CenterX=44.3 CenterY=4.66667 CenterZ=0 NormalX=0 NormalY=0 NormalZ=1 AngleXU=0 Radius=2 StartAngle=1e-16 EndAngle=1.5708
    g7: GeomPoint X=46.3 Y=6.66667 Z=0
  constraints (20):
    c: Coincident(g0,g1)
    c: Coincident(g3,g0)
    c: Horizontal(g0)
    c: Horizontal(g2)
    c: Vertical(g1)
    c: Vertical(g3)
    c: PointOnObject(g0,g-1)
    c: DistanceX(g-1,g0) = 31.3
    c: Distance(g0) = 15
    c: Distance(g3,g5) = 6.66667
    c: PointOnObject(g5,g2)
    c: PointOnObject(g5,g3)
    c: Tangent(g2,g4) = -1.5708
    c: Tangent(g3,g4) = -1.5708
    c: PointOnObject(g7,g1)
    c: PointOnObject(g7,g2)
    c: Tangent(g1,g6) = -1.5708
    c: Tangent(g2,g6) = -1.5708
    c: Equal(g4,g6)
    c: Radius(g4) = 2
FEATURE [PartDesign::Pocket] Pocket005
  BaseFeature = -> MultiTransform
  Length = 5
  Length2 = 100
  Placement = pos=(0,0,0) rot=(0.57735,0.57735,0.57735;2.0944rad)
  Profile = -> Sketch006
  Type = 1
FEATURE [PartDesign::LinearPattern] LinearPattern001
  Direction = -> Y_Axis001
  Length = 280.8
  Occurrences = 5
  Placement = pos=(0,0,0) rot=(0.57735,0.57735,0.57735;2.0944rad)
  expr: Length = (<<Attributes>>.Boxes_Depth - 1) * (70mm + <<Attributes>>.Box_Tolerance)
  expr: Occurrences = <<Attributes>>.Boxes_Depth
FEATURE [PartDesign::MultiTransform] MultiTransform001
  BaseFeature = -> Pocket005
  Originals = -> [Pocket005]
  Placement = pos=(0,0,0) rot=(0.57735,0.57735,0.57735;2.0944rad)
  Transformations = -> [LinearPattern001]
FEATURE [PartDesign::Body] InnerRightWall001
  Group = -> [LCS_0001,Sketch,Pad,Sketch001,Pocket,Sketch002,Pocket001,Sketch003,Pocket002,Sketch004,Pocket003,Sketch005,Pocket004,MultiTransform,LinearPattern,Sketch006,Pocket005,MultiTransform001,LinearPattern001]
  Origin = -> Origin001
  Tip = -> MultiTransform001
FEATURE [App::Part] InnerRightWall
  Group = -> [LCS_0,InnerRightWall001,PropertyBag]
  Origin = -> Origin
---- part OuterFrontWall.FCStd = doc fcstd_36fb5d3701b1 ----
FCSTD DOCUMENT  (FreeCAD 0.19R24291 (Git))
Label: OuterFrontWall
License: All rights reserved
LicenseURL: http://en.wikipedia.org/wiki/All_rights_reserved
objects: Sketcher::SketchObject×4, PartDesign::CoordinateSystem×3, PartDesign::Pocket×2, App::FeaturePython×1, PartDesign::Pad×1, PartDesign::Plane×1, PartDesign::Hole×1, PartDesign::Body×1, App::Part×1
note: 17 computed .brp shape members not serialized (recipe doc carries the construction recipe); baked Part::Feature solids carry a one-line shape summary decoded from their .brp

FEATURE [PartDesign::CoordinateSystem] LCS_0
  AttacherType = Attacher::AttachEngine3D
  MapMode = 2
  Support = -> [X_Axis]
FEATURE [PartDesign::CoordinateSystem] LCS_0001
  AttacherType = Attacher::AttachEngine3D
  MapMode = 2
  Support = -> [X_Axis001]
FEATURE [Sketcher::SketchObject] Sketch
  FullyConstrained = true
  MapMode = 5
  Placement = pos=(0,0,0) rot=(1,0,0;1.5708rad)
  Support = -> [XZ_Plane001]
  expr: Constraints[48] = <<Attributes>>.LogicSpaceCornerRadius
  expr: Constraints[28] = <<Attributes>>.DrawerWidth_DW + <<Attributes>>.SideLengt * 2 - (<<Attributes>>.SideLengt + <<Attributes>>.WallThickness_WT * 2 + <<Attributes>>.LogicSpaceCornerRadius + <<Attributes>>.LogicSpaceWidth)
  expr: Constraints[25] = <<Attributes>>.DrawerHeight_DH - <<Attributes>>.WallThickness_WT / 2
  expr: Constraints[26] = <<Attributes>>.DrawerHeight_DH / 2
  expr: Constraints[9] = <<Attributes>>.DrawerWidth_DW + <<Attributes>>.SideLengt * 2
  expr: Constraints[27] = <<Attributes>>.DrawerWidth_DW + <<Attributes>>.SideLengt * 2 - (<<Attributes>>.SideLengt + <<Attributes>>.WallThickness_WT * 2 + <<Attributes>>.LogicSpaceCornerRadius)
  expr: Constraints[24] = <<Attributes>>.WallThickness_WT / 2
  expr: Constraints[19] = <<Attributes>>.ScrewPreWhole / 2
  expr: Constraints[49] = <<Attributes>>.HandelDimC - (<<Attributes>>.HandelDimC - <<Attributes>>.HandelDimA) / 2
  expr: Constraints[15] = (<<Attributes>>.DrawerWidth_DW + <<Attributes>>.SideLengt * 2) / 2
  expr: Constraints[10] = <<Attributes>>.DrawerHeight_DH
  sketch-geometry (20):
    g0: LineSegment StartX=0 StartY=0 StartZ=0 EndX=450.8 EndY=0 EndZ=0
    g1: LineSegment StartX=450.8 StartY=0 StartZ=0 EndX=450.8 EndY=64 EndZ=0
    g2: LineSegment StartX=450.8 StartY=64 StartZ=0 EndX=0 EndY=64 EndZ=0
    g3: LineSegment StartX=0 StartY=64 StartZ=0 EndX=0 EndY=0 EndZ=0
    g4: LineSegment StartX=165.4 StartY=32 StartZ=0 EndX=225.4 EndY=32 EndZ=0
    g5: LineSegment StartX=225.4 StartY=32 StartZ=0 EndX=285.4 EndY=32 EndZ=0
    g6: Circle CenterX=165.4 CenterY=32 CenterZ=0 NormalX=0 NormalY=0 NormalZ=1 AngleXU=0 Radius=1.5
    g7: Circle CenterX=285.4 CenterY=32 CenterZ=0 NormalX=0 NormalY=0 NormalZ=1 AngleXU=0 Radius=1.5
    g8: LineSegment StartX=300.8 StartY=56.5 StartZ=0 EndX=398.8 EndY=56.5 EndZ=0
    g9: LineSegment StartX=399.8 StartY=55.5 StartZ=0 EndX=399.8 EndY=8.5 EndZ=0
    g10: LineSegment StartX=398.8 StartY=7.5 StartZ=0 EndX=300.8 EndY=7.5 EndZ=0
    g11: LineSegment StartX=299.8 StartY=8.5 StartZ=0 EndX=299.8 EndY=55.5 EndZ=0
    g12: ArcOfCircle CenterX=300.8 CenterY=55.5 CenterZ=0 NormalX=0 NormalY=0 NormalZ=1 AngleXU=0 Radius=1 StartAngle=1.5708 EndAngle=3.14159
    g13: GeomPoint X=299.8 Y=56.5 Z=0
    g14: ArcOfCircle CenterX=398.8 CenterY=55.5 CenterZ=0 NormalX=0 NormalY=0 NormalZ=1 AngleXU=0 Radius=1 StartAngle=0 EndAngle=1.5708
    g15: GeomPoint X=399.8 Y=56.5 Z=0
    g16: ArcOfCircle CenterX=398.8 CenterY=8.5 CenterZ=0 NormalX=0 NormalY=0 NormalZ=1 AngleXU=0 Radius=1 StartAngle=4.71239 EndAngle=6.28319
    g17: GeomPoint X=399.8 Y=7.5 Z=0
    g18: ArcOfCircle CenterX=300.8 CenterY=8.5 CenterZ=0 NormalX=0 NormalY=0 NormalZ=1 AngleXU=0 Radius=1 StartAngle=3.14159 EndAngle=4.71239
    g19: GeomPoint X=299.8 Y=7.5 Z=0
  constraints (50):
    c: Coincident(g0,g1)
    c: Coincident(g1,g2)
    c: Coincident(g2,g3)
    c: Coincident(g3,g0)
    c: Horizontal(g0)
    c: Horizontal(g2)
    c: Vertical(g1)
    c: Vertical(g3)
    c: Coincident(g0,g-1)
    c: DistanceX(g0,g0) = 450.8
    c: DistanceY(g0,g2) = 64
    c: Horizontal(g4)
    c: Coincident(g4,g5)
    c: Horizontal(g5)
    c: Equal(g4,g5)
    c: DistanceX(g0,g4) = 225.4
    c: Coincident(g6,g4)
    c: Coincident(g7,g5)
    c: Equal(g6,g7)
    c: Radius(g6) = 1.5
    c: Horizontal(g8)
    c: Horizontal(g10)
    c: Vertical(g9)
    c: Vertical(g11)
    c: DistanceY(g0,g19) = 7.5
    c: DistanceY(g0,g13) = 56.5
    c: DistanceY(g0,g4) = 32
    c: DistanceX(g0,g17) = 399.8
    c: DistanceX(g0,g19) = 299.8
    c: PointOnObject(g13,g8)
    c: PointOnObject(g13,g11)
    c: Tangent(g8,g12) = 1.5708
    c: Tangent(g11,g12) = 1.5708
    c: PointOnObject(g15,g8)
    c: PointOnObject(g15,g9)
    c: Tangent(g8,g14) = 1.5708
    c: Tangent(g9,g14) = 1.5708
    c: PointOnObject(g17,g9)
    c: PointOnObject(g17,g10)
    c: Tangent(g9,g16) = 1.5708
    c: Tangent(g10,g16) = 1.5708
    c: PointOnObject(g19,g10)
    c: PointOnObject(g19,g11)
    c: Tangent(g10,g18) = 1.5708
    c: Tangent(g11,g18) = 1.5708
    c: Equal(g18,g12)
    c: Equal(g12,g14)
    c: Equal(g14,g16)
    c: Radius(g12) = 1
    c: DistanceX(g6,g7) = 120
FEATURE [App::FeaturePython] PropertyBag  label="Attributes"  # WARN: FeaturePython — macro-defined, semantics opaque (R4)
  BackWidth = 395.8
  Back_Space = 100
  BottomDepth = 365.8
  BottomWidth = 365.8
  Bottom_Height_BH = 4
  Bottom_Space_Height = 20
  Box_Tolerance = 0.2
  Boxes_Depth = 5
  Boxes_Height = 40
  Boxes_Width = 5
  CableChannelHight = 15
  CableChannelRadius = 2
  CustomPropertyGroups = shape | attributes
  DrawerDepth_DD = 465.8
  DrawerHeight_DH = 64
  DrawerWidth_DW = 410.8
  FrontWindowRecessedDepth = 3
  HandelDimA = 100
  HandelDimB = 30
  HandelDimC = 140
  HandelDimD = 70
  HandelDimE = 30
  InnerWallDepth = 358.3
  LogicBoardScrewHeadDiameter = 6
  LogicBoardScrewHeadHeight = 3
  LogicBoardStandoffHoleDiameter = 3
  LogicBoardStandoffHoleSideSpace = 6
  LogicSpaceCornerRadius = 1
  LogicSpaceWidth = 100
  ScrewPreWhole = 3
  ScrewPreWholeDepth = 20
  SideLengt = 20
  WallThickness_WT = 15
  expr: BottomDepth = Boxes_Depth * 70mm + WallThickness_WT + Box_Tolerance * (Boxes_Width - 1)
  expr: DrawerHeight_DH = Boxes_Height + Bottom_Height_BH + Bottom_Space_Height
  expr: BackWidth = DrawerWidth_DW - WallThickness_WT
  expr: DrawerWidth_DW = Boxes_Width * 70mm + WallThickness_WT * 4 + Box_Tolerance * (Boxes_Width - 1)
  expr: BottomWidth = Boxes_Width * 70mm + WallThickness_WT + Box_Tolerance * (Boxes_Width - 1)
  expr: DrawerDepth_DD = Boxes_Depth * 70mm + WallThickness_WT + Back_Space + Box_Tolerance * (Boxes_Width - 1)
  expr: InnerWallDepth = Boxes_Depth * 70mm + WallThickness_WT * 0.5 + Box_Tolerance * (Boxes_Width - 1)
FEATURE [PartDesign::Pad] Pad
  Direction = (1,1,1)
  Length = 15
  Length2 = 100
  Placement = pos=(0,0,0) rot=(1,0,0;1.5708rad)
  Profile = -> Sketch
  Type = 0
  expr: Length = <<Attributes>>.WallThickness_WT
FEATURE [PartDesign::Plane] DatumPlane
  Length = 60
  MapMode = 3
  Placement = pos=(0,0,0) rot=(1,0,0;1.5708rad)
  ResizeMode = 0
  Support = -> [LCS_0]
  Width = 60
FEATURE [Sketcher::SketchObject] Sketch001
  FullyConstrained = true
  MapMode = 5
  Placement = pos=(0,0,0) rot=(1,0,0;1.5708rad)
  Support = -> [DatumPlane]
  expr: Constraints[27] = <<Attributes>>.LogicSpaceCornerRadius
  expr: Constraints[7] = <<Attributes>>.DrawerWidth_DW + <<Attributes>>.SideLengt * 2 - (<<Attributes>>.SideLengt + <<Attributes>>.WallThickness_WT * 2 + <<Attributes>>.LogicSpaceCornerRadius + <<Attributes>>.LogicSpaceWidth) - <<Attributes>>.WallThickness_WT / 4
  expr: Constraints[6] = <<Attributes>>.DrawerWidth_DW + <<Attributes>>.SideLengt * 2 - (<<Attributes>>.SideLengt + <<Attributes>>.WallThickness_WT * 2 + <<Attributes>>.LogicSpaceCornerRadius) + <<Attributes>>.WallThickness_WT / 4
  expr: Constraints[5] = <<Attributes>>.DrawerHeight_DH - <<Attributes>>.WallThickness_WT / 4
  expr: Constraints[4] = <<Attributes>>.WallThickness_WT / 4
  sketch-geometry (12):
    g0: LineSegment StartX=297.05 StartY=60.25 StartZ=0 EndX=402.55 EndY=60.25 EndZ=0
    g1: LineSegment StartX=403.55 StartY=59.25 StartZ=0 EndX=403.55 EndY=4.75 EndZ=0
    g2: LineSegment StartX=402.55 StartY=3.75 StartZ=0 EndX=297.05 EndY=3.75 EndZ=0
    g3: LineSegment StartX=296.05 StartY=4.75 StartZ=0 EndX=296.05 EndY=59.25 EndZ=0
    g4: ArcOfCircle CenterX=297.05 CenterY=59.25 CenterZ=0 NormalX=0 NormalY=0 NormalZ=1 AngleXU=0 Radius=1 StartAngle=1.5708 EndAngle=3.14159
    g5: GeomPoint X=296.05 Y=60.25 Z=0
    g6: ArcOfCircle CenterX=402.55 CenterY=59.25 CenterZ=0 NormalX=0 NormalY=0 NormalZ=1 AngleXU=0 Radius=1 StartAngle=-2.93e-14 EndAngle=1.5708
    g7: GeomPoint X=403.55 Y=60.25 Z=0
    g8: ArcOfCircle CenterX=402.55 CenterY=4.75 CenterZ=0 NormalX=0 NormalY=0 NormalZ=1 AngleXU=0 Radius=1 StartAngle=4.71239 EndAngle=6.28319
    g9: GeomPoint X=403.55 Y=3.75 Z=0
    g10: ArcOfCircle CenterX=297.05 CenterY=4.75 CenterZ=0 NormalX=0 NormalY=0 NormalZ=1 AngleXU=0 Radius=1 StartAngle=3.14159 EndAngle=4.71239
    g11: GeomPoint X=296.05 Y=3.75 Z=0
  constraints (28):
    c: Horizontal(g0)
    c: Horizontal(g2)
    c: Vertical(g1)
    c: Vertical(g3)
    c: DistanceY(g-1,g11) = 3.75
    c: DistanceY(g-1,g5) = 60.25
    c: DistanceX(g-1,g9) = 403.55
    c: DistanceX(g-1,g11) = 296.05
    c: PointOnObject(g5,g0)
    c: PointOnObject(g5,g3)
    c: Tangent(g0,g4) = 1.5708
    c: Tangent(g3,g4) = 1.5708
    c: PointOnObject(g7,g0)
    c: PointOnObject(g7,g1)
    c: Tangent(g0,g6) = 1.5708
    c: Tangent(g1,g6) = 1.5708
    c: PointOnObject(g9,g1)
    c: PointOnObject(g9,g2)
    c: Tangent(g1,g8) = 1.5708
    c: Tangent(g2,g8) = 1.5708
    c: PointOnObject(g11,g2)
    c: PointOnObject(g11,g3)
    c: Tangent(g2,g10) = 1.5708
    c: Tangent(g3,g10) = 1.5708
    c: Equal(g10,g4)
    c: Equal(g4,g6)
    c: Equal(g6,g8)
    c: Radius(g6) = 1
FEATURE [PartDesign::Pocket] Pocket
  BaseFeature = -> Pad
  Length = 12
  Length2 = 100
  Placement = pos=(0,0,0) rot=(1,0,0;1.5708rad)
  Profile = -> Sketch001
  Reversed = true
  Type = 0
  expr: Length = <<Attributes>>.WallThickness_WT - <<Attributes>>.FrontWindowRecessedDepth
FEATURE [Sketcher::SketchObject] Sketch002
  FullyConstrained = true
  MapMode = 5
  Placement = pos=(0,0,0) rot=(1,0,0;1.5708rad)
  Support = -> [DatumPlane]
  expr: Constraints[49] = <<Attributes>>.LogicSpaceCornerRadius
  expr: Constraints[5] = <<Attributes>>.DrawerHeight_DH - <<Attributes>>.WallThickness_WT / 2 - (<<Attributes>>.DrawerHeight_DH - <<Attributes>>.WallThickness_WT - <<Attributes>>.Bottom_Space_Height - <<Attributes>>.Bottom_Height_BH) / 2 - <<Attributes>>.CableChannelHight / 2
  expr: Constraints[6] = <<Attributes>>.DrawerHeight_DH - <<Attributes>>.WallThickness_WT / 2 - (<<Attributes>>.DrawerHeight_DH - <<Attributes>>.WallThickness_WT - <<Attributes>>.Bottom_Space_Height - <<Attributes>>.Bottom_Height_BH) / 2 + <<Attributes>>.CableChannelHight / 2
  expr: Constraints[12] = <<Attributes>>.DrawerWidth_DW + <<Attributes>>.SideLengt
  expr: Constraints[4] = <<Attributes>>.DrawerWidth_DW + <<Attributes>>.SideLengt * 2 - (<<Attributes>>.SideLengt + <<Attributes>>.WallThickness_WT * 2 + <<Attributes>>.LogicSpaceCornerRadius + <<Attributes>>.LogicSpaceWidth) - <<Attributes>>.WallThickness_WT / 4
  expr: Constraints[3] = <<Attributes>>.SideLengt
  expr: Constraints[13] = <<Attributes>>.DrawerWidth_DW + <<Attributes>>.SideLengt - <<Attributes>>.WallThickness_WT * 2 - <<Attributes>>.LogicSpaceCornerRadius + <<Attributes>>.WallThickness_WT / 4
  sketch-geometry (24):
    g0: LineSegment StartX=21 StartY=51.5 StartZ=0 EndX=295.05 EndY=51.5 EndZ=0
    g1: LineSegment StartX=295.05 StartY=36.5 StartZ=0 EndX=21 EndY=36.5 EndZ=0
    g2: LineSegment StartX=20 StartY=37.5 StartZ=0 EndX=20 EndY=50.5 EndZ=0
    g3: LineSegment StartX=404.55 StartY=51.5 StartZ=0 EndX=429.8 EndY=51.5 EndZ=0
    g4: LineSegment StartX=430.8 StartY=50.5 StartZ=0 EndX=430.8 EndY=37.5 EndZ=0
    g5: LineSegment StartX=429.8 StartY=36.5 StartZ=0 EndX=404.55 EndY=36.5 EndZ=0
    g6: LineSegment StartX=296.05 StartY=52.5 StartZ=0 EndX=403.55 EndY=52.5 EndZ=0
    g7: LineSegment StartX=296.05 StartY=35.5 StartZ=0 EndX=403.55 EndY=35.5 EndZ=0
    g8: ArcOfCircle CenterX=295.05 CenterY=52.5 CenterZ=0 NormalX=0 NormalY=0 NormalZ=1 AngleXU=0 Radius=1 StartAngle=4.71239 EndAngle=6.28319
    g9: GeomPoint X=296.05 Y=51.5 Z=0
    g10: ArcOfCircle CenterX=404.55 CenterY=52.5 CenterZ=0 NormalX=0 NormalY=0 NormalZ=1 AngleXU=0 Radius=1 StartAngle=3.14159 EndAngle=4.71239
    g11: GeomPoint X=403.55 Y=51.5 Z=0
    g12: ArcOfCircle CenterX=404.55 CenterY=35.5 CenterZ=0 NormalX=0 NormalY=0 NormalZ=1 AngleXU=0 Radius=1 StartAngle=1.5708 EndAngle=3.14159
    g13: GeomPoint X=403.55 Y=36.5 Z=0
    g14: ArcOfCircle CenterX=295.05 CenterY=35.5 CenterZ=0 NormalX=0 NormalY=0 NormalZ=1 AngleXU=0 Radius=1 StartAngle=1.42e-14 EndAngle=1.5708
    g15: GeomPoint X=296.05 Y=36.5 Z=0
    g16: ArcOfCircle CenterX=429.8 CenterY=50.5 CenterZ=0 NormalX=0 NormalY=0 NormalZ=1 AngleXU=0 Radius=1 StartAngle=4e-16 EndAngle=1.5708
    g17: GeomPoint X=430.8 Y=51.5 Z=0
    g18: ArcOfCircle CenterX=429.8 CenterY=37.5 CenterZ=0 NormalX=0 NormalY=0 NormalZ=1 AngleXU=0 Radius=1 StartAngle=4.71239 EndAngle=6.28319
    g19: GeomPoint X=430.8 Y=36.5 Z=0
    g20: ArcOfCircle CenterX=21 CenterY=50.5 CenterZ=0 NormalX=0 NormalY=0 NormalZ=1 AngleXU=0 Radius=1 StartAngle=1.5708 EndAngle=3.14159
    g21: GeomPoint X=20 Y=51.5 Z=0
    g22: ArcOfCircle CenterX=21 CenterY=37.5 CenterZ=0 NormalX=0 NormalY=0 NormalZ=1 AngleXU=0 Radius=1 StartAngle=3.14159 EndAngle=4.71239
    g23: GeomPoint X=20 Y=36.5 Z=0
  constraints (60):
    c: Horizontal(g0)
    c: Horizontal(g1)
    c: Vertical(g2)
    c: DistanceX(g-1,g23) = 20
    c: DistanceX(g-1,g15) = 296.05
    c: DistanceY(g-1,g23) = 36.5
    c: DistanceY(g-1,g21) = 51.5
    c: Horizontal(g3)
    c: Horizontal(g5)
    c: Vertical(g4)
    c: Horizontal(g11,g9)
    c: Horizontal(g13,g15)
    c: DistanceX(g-1,g17) = 430.8
    c: DistanceX(g-1,g13) = 403.55
    c: Vertical(g9,g15)
    c: Vertical(g11,g13)
    c: Horizontal(g6)
    c: Horizontal(g7)
    c: PointOnObject(g9,g0)
    c: Tangent(g0,g8) = -1.5708
    c: PointOnObject(g11,g3)
    c: Tangent(g3,g10) = -1.5708
    c: PointOnObject(g13,g5)
    c: Tangent(g5,g12) = -1.5708
    c: PointOnObject(g15,g1)
    c: Tangent(g1,g14) = -1.5708
    c: PointOnObject(g17,g3)
    c: PointOnObject(g17,g4)
    c: Tangent(g3,g16) = 1.5708
    c: Tangent(g4,g16) = 1.5708
    c: PointOnObject(g19,g4)
    c: PointOnObject(g19,g5)
    c: Tangent(g4,g18) = 1.5708
    c: Tangent(g5,g18) = 1.5708
    c: PointOnObject(g21,g0)
    c: PointOnObject(g21,g2)
    c: Tangent(g0,g20) = 1.5708
    c: Tangent(g2,g20) = 1.5708
    c: PointOnObject(g23,g1)
    c: PointOnObject(g23,g2)
    c: Tangent(g1,g22) = 1.5708
    c: Tangent(g2,g22) = 1.5708
    c: Equal(g22,g20)
    c: Equal(g20,g8)
    c: Equal(g8,g14)
    c: Equal(g14,g10)
    c: Equal(g10,g12)
    c: Equal(g12,g16)
    c: Equal(g16,g18)
    c: Radius(g10) = 1
    c: Horizontal(g12,g12)
    c: Horizontal(g10,g10)
    c: Coincident(g6,g10)
    c: Coincident(g8,g6)
    c: Vertical(g9,g6)
    c: Vertical(g11,g6)
    c: Vertical(g13,g12)
    c: Coincident(g12,g7)
    c: Coincident(g14,g7)
    c: Vertical(g7,g15)
FEATURE [PartDesign::Pocket] Pocket001
  BaseFeature = -> Pocket
  Length = 7.5
  Length2 = 100
  Placement = pos=(0,0,0) rot=(1,0,0;1.5708rad)
  Profile = -> Sketch002
  Reversed = true
  Type = 0
  expr: Length = <<Attributes>>.WallThickness_WT / 2
FEATURE [Sketcher::SketchObject] Sketch003
  FullyConstrained = true
  MapMode = 5
  Placement = pos=(0,0,0) rot=(1,0,0;1.5708rad)
  Support = -> [DatumPlane]
  expr: Constraints[25] = <<Attributes>>.ScrewPreWhole / 2
  expr: Constraints[12] = <<Attributes>>.DrawerHeight_DH - <<Attributes>>.WallThickness_WT / 2
  expr: Constraints[11] = <<Attributes>>.DrawerHeight_DH - <<Attributes>>.WallThickness_WT - <<Attributes>>.Bottom_Space_Height - <<Attributes>>.Bottom_Height_BH
  expr: Constraints[13] = <<Attributes>>.DrawerWidth_DW + <<Attributes>>.SideLengt * 1.5
  expr: Constraints[7] = <<Attributes>>.Bottom_Space_Height / 2
  expr: Constraints[6] = <<Attributes>>.SideLengt / 2
  sketch-geometry (10):
    g0: LineSegment StartX=10 StartY=56.5 StartZ=0 EndX=10 EndY=31.5 EndZ=0
    g1: LineSegment StartX=10 StartY=31.5 StartZ=0 EndX=10 EndY=10 EndZ=0
    g2: LineSegment StartX=440.8 StartY=56.5 StartZ=0 EndX=440.8 EndY=31.5 EndZ=0
    g3: LineSegment StartX=440.8 StartY=31.5 StartZ=0 EndX=440.8 EndY=10 EndZ=0
    g4: Circle CenterX=10 CenterY=56.5 CenterZ=0 NormalX=0 NormalY=0 NormalZ=1 AngleXU=0 Radius=1.5
    g5: Circle CenterX=10 CenterY=31.5 CenterZ=0 NormalX=0 NormalY=0 NormalZ=1 AngleXU=0 Radius=1.5
    g6: Circle CenterX=10 CenterY=10 CenterZ=0 NormalX=0 NormalY=0 NormalZ=1 AngleXU=0 Radius=1.5
    g7: Circle CenterX=440.8 CenterY=56.5 CenterZ=0 NormalX=0 NormalY=0 NormalZ=1 AngleXU=0 Radius=1.5
    g8: Circle CenterX=440.8 CenterY=31.5 CenterZ=0 NormalX=0 NormalY=0 NormalZ=1 AngleXU=0 Radius=1.5
    g9: Circle CenterX=440.8 CenterY=10 CenterZ=0 NormalX=0 NormalY=0 NormalZ=1 AngleXU=0 Radius=1.5
  constraints (26):
    c: Vertical(g0)
    c: Coincident(g0,g1)
    c: Vertical(g1)
    c: Vertical(g2)
    c: Coincident(g2,g3)
    c: Vertical(g3)
    c: DistanceX(g-1,g1) = 10
    c: DistanceY(g-1,g1) = 10
    c: Horizontal(g1,g3)
    c: Equal(g3,g1)
    c: Equal(g0,g2)
    c: Distance(g0) = 25
    c: DistanceY(g-1,g0) = 56.5
    c: DistanceX(g-1,g3) = 440.8
    c: Coincident(g4,g0)
    c: Coincident(g5,g0)
    c: Coincident(g6,g1)
    c: Coincident(g7,g2)
    c: Coincident(g8,g2)
    c: Coincident(g9,g3)
    c: Equal(g4,g5)
    c: Equal(g5,g6)
    c: Equal(g6,g7)
    c: Equal(g7,g8)
    c: Equal(g8,g9)
    c: Radius(g4) = 1.5
FEATURE [PartDesign::Hole] Hole
  BaseFeature = -> Pocket001
  Depth = 7.5
  DepthType = 0
  Diameter = 3
  DrillForDepth = false
  DrillPoint = 1
  DrillPointAngle = 118
  HoleCutCountersinkAngle = 90
  HoleCutCustomValues = false
  HoleCutDepth = 0
  HoleCutDiameter = 6.1
  HoleCutType = 0
  ModelActualThread = false
  Placement = pos=(0,0,0) rot=(1,0,0;1.5708rad)
  Profile = -> Sketch003
  Reversed = true
  Tapered = false
  TaperedAngle = 90
  ThreadAngle = 0
  ThreadClass = 0
  ThreadCutOffInner = 0
  ThreadCutOffOuter = 0
  ThreadDirection = 0
  ThreadFit = 0
  ThreadPitch = 0
  ThreadSize = 0
  ThreadType = 0
  Threaded = false
  expr: Depth = <<Attributes>>.WallThickness_WT / 2
  expr: Diameter = <<Attributes>>.ScrewPreWhole
FEATURE [PartDesign::Body] OuterFrontWall001
  Group = -> [LCS_0001,Sketch,Pad,DatumPlane,Sketch001,Pocket,Sketch002,Pocket001,Sketch003,Hole]
  Origin = -> Origin001
  Tip = -> Hole
FEATURE [PartDesign::CoordinateSystem] OuterFrontWall_FrontWindow  label="OuterFrontWall-FrontWindow"
  AttacherType = Attacher::AttachEngine3D
  AttachmentOffset = pos=(349.8,-15,32) rot=(0,0,1;0rad)
  MapMode = 2
  Placement = pos=(349.8,-15,32) rot=(0,0,1;0rad)
  Support = -> [LCS_0]
  expr: .AttachmentOffset.Base.z = <<Attributes>>.DrawerHeight_DH / 2
  expr: .AttachmentOffset.Base.y = -<<Attributes>>.WallThickness_WT
  expr: .AttachmentOffset.Base.x = <<Attributes>>.DrawerWidth_DW + <<Attributes>>.SideLengt * 2 - (<<Attributes>>.SideLengt + <<Attributes>>.WallThickness_WT * 2 + <<Attributes>>.LogicSpaceCornerRadius + <<Attributes>>.LogicSpaceWidth / 2)
FEATURE [App::Part] OuterFrontWall
  Group = -> [LCS_0,OuterFrontWall001,PropertyBag,OuterFrontWall_FrontWindow]
  Origin = -> Origin
---- part OuterRightWall.FCStd = doc fcstd_2889e779a45c ----
FCSTD DOCUMENT  (FreeCAD 0.19R24291 (Git))
Label: OuterRightWall
License: All rights reserved
LicenseURL: http://en.wikipedia.org/wiki/All_rights_reserved
objects: Sketcher::SketchObject×7, PartDesign::Pocket×6, PartDesign::CoordinateSystem×2, App::FeaturePython×1, PartDesign::Pad×1, PartDesign::LinearPattern×1, PartDesign::MultiTransform×1, PartDesign::Body×1, App::Part×1
note: 26 computed .brp shape members not serialized (recipe doc carries the construction recipe); baked Part::Feature solids carry a one-line shape summary decoded from their .brp

FEATURE [PartDesign::CoordinateSystem] LCS_0
  AttacherType = Attacher::AttachEngine3D
  MapMode = 2
  Support = -> [X_Axis]
FEATURE [PartDesign::CoordinateSystem] LCS_0001
  AttacherType = Attacher::AttachEngine3D
  MapMode = 2
  Support = -> [X_Axis001]
FEATURE [Sketcher::SketchObject] Sketch
  FullyConstrained = true
  MapMode = 5
  Placement = pos=(0,0,0) rot=(0.57735,0.57735,0.57735;2.0944rad)
  Support = -> [YZ_Plane001]
  expr: Constraints[10] = <<Attributes>>.DrawerHeight_DH
  expr: Constraints[9] = <<Attributes>>.DrawerDepth_DD + <<Attributes>>.WallThickness_WT / 2
  sketch-geometry (4):
    g0: LineSegment StartX=0 StartY=0 StartZ=0 EndX=507.5 EndY=0 EndZ=0
    g1: LineSegment StartX=507.5 StartY=0 StartZ=0 EndX=507.5 EndY=64 EndZ=0
    g2: LineSegment StartX=507.5 StartY=64 StartZ=0 EndX=0 EndY=64 EndZ=0
    g3: LineSegment StartX=0 StartY=64 StartZ=0 EndX=0 EndY=0 EndZ=0
  constraints (11):
    c: Coincident(g0,g1)
    c: Coincident(g1,g2)
    c: Coincident(g2,g3)
    c: Coincident(g3,g0)
    c: Horizontal(g0)
    c: Horizontal(g2)
    c: Vertical(g1)
    c: Vertical(g3)
    c: Coincident(g0,g-1)
    c: Distance(g0) = 507.5
    c: DistanceY(g0,g2) = 64
FEATURE [App::FeaturePython] PropertyBag  label="Attributes"  # WARN: FeaturePython — macro-defined, semantics opaque (R4)
  BackWidth = 395.8
  Back_Space = 134.2
  BottomDepth = 365.8
  BottomWidth = 365.8
  Bottom_Height_BH = 4
  Bottom_Space_Height = 20
  Box_Tolerance = 0.2
  Boxes_Depth = 5
  Boxes_Height = 40
  Boxes_Width = 5
  CableChannelHight = 15
  CableChannelRadius = 2
  CustomPropertyGroups = shape | attributes
  DrawerDepth_DD = 500
  DrawerHeight_DH = 64
  DrawerWidth_DW = 410.8
  InnerWallDepth = 358.3
  ScrewPreWhole = 3
  ScrewPreWholeDepth = 20
  WallThickness_WT = 15
  expr: BottomDepth = Boxes_Depth * 70mm + WallThickness_WT + Box_Tolerance * (Boxes_Width - 1)
  expr: DrawerHeight_DH = Boxes_Height + Bottom_Height_BH + Bottom_Space_Height
  expr: BackWidth = DrawerWidth_DW - WallThickness_WT
  expr: DrawerWidth_DW = Boxes_Width * 70mm + WallThickness_WT * 4 + Box_Tolerance * (Boxes_Width - 1)
  expr: BottomWidth = Boxes_Width * 70mm + WallThickness_WT + Box_Tolerance * (Boxes_Width - 1)
  expr: DrawerDepth_DD = Boxes_Depth * 70mm + WallThickness_WT + Back_Space + Box_Tolerance * (Boxes_Width - 1)
  expr: InnerWallDepth = Boxes_Depth * 70mm + WallThickness_WT * 0.5 + Box_Tolerance * (Boxes_Width - 1)
FEATURE [PartDesign::Pad] Pad
  Direction = (1,1,1)
  Length = 15
  Length2 = 100
  Placement = pos=(0,0,0) rot=(0.57735,0.57735,0.57735;2.0944rad)
  Profile = -> Sketch
  Type = 0
  expr: Length = <<Attributes>>.WallThickness_WT
FEATURE [Sketcher::SketchObject] Sketch001
  FullyConstrained = true
  MapMode = 5
  Placement = pos=(-6.34e-14,0,0) rot=(0.57735,0.57735,-0.57735;4.18879rad)
  Support = -> [Pad]
  expr: Constraints[17] = (<<Attributes>>.DrawerHeight_DH - <<Attributes>>.WallThickness_WT - <<Attributes>>.Bottom_Space_Height - <<Attributes>>.Bottom_Height_BH) / 2
  expr: Constraints[16] = <<Attributes>>.DrawerHeight_DH - <<Attributes>>.WallThickness_WT / 2
  expr: Constraints[7] = <<Attributes>>.DrawerDepth_DD + <<Attributes>>.WallThickness_WT / 2
  expr: Constraints[6] = <<Attributes>>.CableChannelHight
  sketch-geometry (6):
    g0: LineSegment StartX=0 StartY=-36.5 StartZ=0 EndX=507.5 EndY=-36.5 EndZ=0
    g1: LineSegment StartX=507.5 StartY=-36.5 StartZ=0 EndX=507.5 EndY=-51.5 EndZ=0
    g2: LineSegment StartX=507.5 StartY=-51.5 StartZ=0 EndX=0 EndY=-51.5 EndZ=0
    g3: LineSegment StartX=0 StartY=-51.5 StartZ=0 EndX=0 EndY=-44 EndZ=0
    g4: LineSegment StartX=0 StartY=-44 StartZ=0 EndX=0 EndY=-36.5 EndZ=0
    g5: LineSegment StartX=0 StartY=0 StartZ=0 EndX=0 EndY=-56.5 EndZ=0
  constraints (18):
    c: Coincident(g0,g1)
    c: Coincident(g1,g2)
    c: Horizontal(g0)
    c: Horizontal(g2)
    c: Vertical(g1)
    c: PointOnObject(g0,g-2)
    c: DistanceY(g2,g0) = 15
    c: DistanceX(g0,g0) = 507.5
    c: Coincident(g2,g3)
    c: Vertical(g3)
    c: Coincident(g3,g4)
    c: Coincident(g4,g0)
    c: Vertical(g4)
    c: Equal(g3,g4)
    c: Coincident(g5,g-1)
    c: Vertical(g5)
    c: Distance(g5) = 56.5
    c: DistanceY(g5,g3) = 12.5
FEATURE [PartDesign::Pocket] Pocket
  BaseFeature = -> Pad
  Length = 7.5
  Length2 = 100
  Placement = pos=(0,0,0) rot=(0.57735,0.57735,0.57735;2.0944rad)
  Profile = -> Sketch001
  Type = 0
  expr: Length = <<Attributes>>.WallThickness_WT / 2
FEATURE [Sketcher::SketchObject] Sketch002
  FullyConstrained = true
  MapMode = 5
  Placement = pos=(-1.269e-13,0,0) rot=(-0.57735,-0.57735,0.57735;2.0944rad)
  Support = -> [Pocket]
  expr: Constraints[23] = (<<Attributes>>.WallThickness_WT / 2 + 70mm + <<Attributes>>.Box_Tolerance / 2) / 2 - <<Attributes>>.CableChannelHight / 2
  expr: Constraints[22] = <<Attributes>>.DrawerHeight_DH - <<Attributes>>.WallThickness_WT / 2 - (<<Attributes>>.DrawerHeight_DH - <<Attributes>>.WallThickness_WT - <<Attributes>>.Bottom_Space_Height - <<Attributes>>.Bottom_Height_BH) / 2 - <<Attributes>>.CableChannelHight / 2
  expr: Constraints[21] = <<Attributes>>.CableChannelRadius
  expr: Constraints[6] = <<Attributes>>.CableChannelHight
  sketch-geometry (8):
    g0: LineSegment StartX=31.3 StartY=0 StartZ=0 EndX=46.3 EndY=0 EndZ=0
    g1: LineSegment StartX=46.3 StartY=0 StartZ=0 EndX=46.3 EndY=-34.5 EndZ=0
    g2: LineSegment StartX=31.3 StartY=-34.5 StartZ=0 EndX=31.3 EndY=0 EndZ=0
    g3: ArcOfCircle CenterX=29.3 CenterY=-34.5 CenterZ=0 NormalX=0 NormalY=0 NormalZ=1 AngleXU=0 Radius=2 StartAngle=4.71239 EndAngle=6.28319
    g4: ArcOfCircle CenterX=48.3 CenterY=-34.5 CenterZ=0 NormalX=0 NormalY=0 NormalZ=1 AngleXU=0 Radius=2 StartAngle=3.14159 EndAngle=4.71239
    g5: LineSegment StartX=46.3 StartY=-34.5 StartZ=0 EndX=48.3 EndY=-34.5 EndZ=0
    g6: LineSegment StartX=29.3 StartY=-34.5 StartZ=0 EndX=31.3 EndY=-34.5 EndZ=0
    g7: LineSegment StartX=29.3 StartY=-36.5 StartZ=0 EndX=48.3 EndY=-36.5 EndZ=0
  constraints (24):
    c: Coincident(g0,g1)
    c: Coincident(g2,g0)
    c: Horizontal(g0)
    c: Vertical(g1)
    c: Vertical(g2)
    c: PointOnObject(g0,g-1)
    c: Distance(g0) = 15
    c: Coincident(g3,g2)
    c: Coincident(g4,g1)
    c: Angle(g4) = 1.5708
    c: Angle(g3) = 1.5708
    c: Coincident(g5,g1)
    c: Coincident(g5,g4)
    c: Perpendicular(g1,g5)
    c: Coincident(g6,g3)
    c: Coincident(g6,g2)
    c: Perpendicular(g2,g6)
    c: Equal(g6,g5)
    c: Coincident(g7,g3)
    c: Horizontal(g7)
    c: Coincident(g7,g4)
    c: Radius(g3) = 2
    c: DistanceY(g3,g0) = 36.5
    c: DistanceX(g-1,g0) = 31.3
FEATURE [PartDesign::Pocket] Pocket001
  BaseFeature = -> Pocket
  Length = 3.75
  Length2 = 100
  Placement = pos=(0,0,0) rot=(0.57735,0.57735,0.57735;2.0944rad)
  Profile = -> Sketch002
  Type = 0
  expr: Length = <<Attributes>>.WallThickness_WT / 4
FEATURE [PartDesign::LinearPattern] LinearPattern
  Direction = -> Sketch002 [H_Axis]
  Length = 280.8
  Occurrences = 5
  Placement = pos=(0,0,0) rot=(0.57735,0.57735,0.57735;2.0944rad)
  expr: Length = (<<Attributes>>.Boxes_Depth - 1) * (70mm + <<Attributes>>.Box_Tolerance)
  expr: Occurrences = <<Attributes>>.Boxes_Depth
FEATURE [PartDesign::MultiTransform] MultiTransform
  BaseFeature = -> Pocket001
  Originals = -> [Pocket001]
  Placement = pos=(0,0,0) rot=(0.57735,0.57735,0.57735;2.0944rad)
  Transformations = -> [LinearPattern]
FEATURE [Sketcher::SketchObject] Sketch003
  FullyConstrained = true
  MapMode = 5
  Placement = pos=(-1.903e-13,0,0) rot=(-0.57735,-0.57735,0.57735;2.0944rad)
  Support = -> [MultiTransform]
  expr: Constraints[10] = <<Attributes>>.InnerWallDepth
  expr: Constraints[9] = <<Attributes>>.DrawerHeight_DH
  expr: Constraints[11] = <<Attributes>>.WallThickness_WT + <<Attributes>>.InnerWallDepth
  sketch-geometry (4):
    g0: LineSegment StartX=358.3 StartY=0 StartZ=0 EndX=373.3 EndY=0 EndZ=0
    g1: LineSegment StartX=373.3 StartY=0 StartZ=0 EndX=373.3 EndY=-64 EndZ=0
    g2: LineSegment StartX=373.3 StartY=-64 StartZ=0 EndX=358.3 EndY=-64 EndZ=0
    g3: LineSegment StartX=358.3 StartY=-64 StartZ=0 EndX=358.3 EndY=0 EndZ=0
  constraints (12):
    c: Coincident(g0,g1)
    c: Coincident(g1,g2)
    c: Coincident(g2,g3)
    c: Coincident(g3,g0)
    c: Horizontal(g0)
    c: Horizontal(g2)
    c: Vertical(g1)
    c: Vertical(g3)
    c: PointOnObject(g0,g-1)
    c: DistanceY(g2,g0) = 64
    c: DistanceX(g-1,g0) = 358.3
    c: DistanceX(g-1,g0) = 373.3
FEATURE [PartDesign::Pocket] Pocket002
  BaseFeature = -> MultiTransform
  Length = 7.5
  Length2 = 100
  Placement = pos=(0,0,0) rot=(0.57735,0.57735,0.57735;2.0944rad)
  Profile = -> Sketch003
  Type = 0
  expr: Length = <<Attributes>>.WallThickness_WT / 2
FEATURE [Sketcher::SketchObject] Sketch004
  FullyConstrained = true
  MapMode = 5
  Placement = pos=(-2.538e-13,0,0) rot=(-0.57735,-0.57735,0.57735;2.0944rad)
  Support = -> [Pocket002]
  expr: Constraints[12] = <<Attributes>>.DrawerHeight_DH - <<Attributes>>.WallThickness_WT - <<Attributes>>.Bottom_Space_Height - <<Attributes>>.Bottom_Height_BH
  expr: Constraints[11] = <<Attributes>>.ScrewPreWhole / 2
  expr: Constraints[5] = <<Attributes>>.InnerWallDepth + <<Attributes>>.WallThickness_WT / 2
  expr: Constraints[4] = <<Attributes>>.Bottom_Space_Height / 2
  expr: Constraints[3] = <<Attributes>>.DrawerHeight_DH - <<Attributes>>.WallThickness_WT / 2
  sketch-geometry (5):
    g0: LineSegment StartX=365.8 StartY=-10 StartZ=0 EndX=365.8 EndY=-31.5 EndZ=0
    g1: LineSegment StartX=365.8 StartY=-31.5 StartZ=0 EndX=365.8 EndY=-56.5 EndZ=0
    g2: Circle CenterX=365.8 CenterY=-10 CenterZ=0 NormalX=0 NormalY=0 NormalZ=1 AngleXU=0 Radius=1.5
    g3: Circle CenterX=365.8 CenterY=-31.5 CenterZ=0 NormalX=0 NormalY=0 NormalZ=1 AngleXU=0 Radius=1.5
    g4: Circle CenterX=365.8 CenterY=-56.5 CenterZ=0 NormalX=0 NormalY=0 NormalZ=1 AngleXU=0 Radius=1.5
  constraints (13):
    c: Coincident(g0,g1)
    c: Vertical(g1)
    c: Vertical(g0)
    c: DistanceY(g1,g-1) = 56.5
    c: DistanceY(g0,g-1) = 10
    c: DistanceX(g-1,g0) = 365.8
    c: Coincident(g2,g0)
    c: Coincident(g3,g0)
    c: Coincident(g4,g1)
    c: Equal(g4,g3)
    c: Equal(g3,g2)
    c: Radius(g2) = 1.5
    c: DistanceY(g1,g1) = 25
FEATURE [PartDesign::Pocket] Pocket003
  BaseFeature = -> Pocket002
  Length = 5
  Length2 = 100
  Midplane = true
  Placement = pos=(0,0,0) rot=(0.57735,0.57735,0.57735;2.0944rad)
  Profile = -> Sketch004
  Type = 1
FEATURE [Sketcher::SketchObject] Sketch005
  FullyConstrained = true
  MapMode = 5
  Placement = pos=(0,-5.68e-14,0) rot=(0.57735,0.57735,-0.57735;2.0944rad)
  Support = -> [Pocket003]
  expr: Constraints[3] = <<Attributes>>.WallThickness_WT / 2
  expr: Constraints[4] = <<Attributes>>.Bottom_Space_Height / 2
  expr: Constraints[5] = <<Attributes>>.DrawerHeight_DH - <<Attributes>>.WallThickness_WT / 2
  expr: Constraints[11] = <<Attributes>>.ScrewPreWhole / 2
  expr: Constraints[12] = <<Attributes>>.DrawerHeight_DH - <<Attributes>>.WallThickness_WT - <<Attributes>>.Bottom_Space_Height - <<Attributes>>.Bottom_Height_BH
  sketch-geometry (5):
    g0: LineSegment StartX=-10 StartY=7.5 StartZ=0 EndX=-31.5 EndY=7.5 EndZ=0
    g1: LineSegment StartX=-31.5 StartY=7.5 StartZ=0 EndX=-56.5 EndY=7.5 EndZ=0
    g2: Circle CenterX=-56.5 CenterY=7.5 CenterZ=0 NormalX=0 NormalY=0 NormalZ=1 AngleXU=0 Radius=1.5
    g3: Circle CenterX=-31.5 CenterY=7.5 CenterZ=0 NormalX=0 NormalY=0 NormalZ=1 AngleXU=0 Radius=1.5
    g4: Circle CenterX=-10 CenterY=7.5 CenterZ=0 NormalX=0 NormalY=0 NormalZ=1 AngleXU=0 Radius=1.5
  constraints (13):
    c: Horizontal(g0)
    c: Coincident(g0,g1)
    c: Horizontal(g1)
    c: DistanceY(g-1,g0) = 7.5
    c: DistanceX(g0,g-1) = 10
    c: DistanceX(g1,g-1) = 56.5
    c: Coincident(g2,g1)
    c: Coincident(g3,g0)
    c: Coincident(g4,g0)
    c: Equal(g4,g3)
    c: Equal(g3,g2)
    c: Radius(g2) = 1.5
    c: Distance(g1) = 25
FEATURE [PartDesign::Pocket] Pocket004
  BaseFeature = -> Pocket003
  Length = 20
  Length2 = 100
  Placement = pos=(0,0,0) rot=(0.57735,0.57735,0.57735;2.0944rad)
  Profile = -> Sketch005
  Type = 0
  expr: Length = <<Attributes>>.ScrewPreWholeDepth
FEATURE [Sketcher::SketchObject] Sketch006
  FullyConstrained = true
  MapMode = 5
  Placement = pos=(-3.172e-13,0,0) rot=(-0.57735,-0.57735,0.57735;2.0944rad)
  Support = -> [Pocket003]
  expr: Constraints[8] = <<Attributes>>.DrawerHeight_DH - <<Attributes>>.WallThickness_WT - <<Attributes>>.Bottom_Space_Height - <<Attributes>>.Bottom_Height_BH
  expr: Constraints[9] = <<Attributes>>.Bottom_Space_Height / 2
  expr: Constraints[10] = <<Attributes>>.DrawerHeight_DH - <<Attributes>>.WallThickness_WT / 2
  expr: Constraints[11] = <<Attributes>>.ScrewPreWhole / 2
  expr: Constraints[12] = ((<<Attributes>>.WallThickness_WT / 2 + 70mm + <<Attributes>>.Box_Tolerance / 2) / 2 - <<Attributes>>.CableChannelHight / 2) / 2
  expr: Constraints[25] = (<<Attributes>>.WallThickness_WT / 2 + 70mm + <<Attributes>>.Box_Tolerance / 2) / 2 - <<Attributes>>.CableChannelHight / 2 + <<Attributes>>.CableChannelHight / 2 + (<<Attributes>>.Box_Tolerance + 70mm) * (<<Attributes>>.Boxes_Depth - 1) + ((<<Attributes>>.WallThickness_WT / 2 + 70mm + <<Attributes>>.Box_Tolerance / 2) / 2 - <<Attributes>>.CableChannelHight / 2) / 2 + <<Attributes>>.CableChannelHight / 2
  sketch-geometry (10):
    g0: LineSegment StartX=15.65 StartY=-10 StartZ=0 EndX=15.65 EndY=-31.5 EndZ=0
    g1: LineSegment StartX=15.65 StartY=-31.5 StartZ=0 EndX=15.65 EndY=-56.5 EndZ=0
    g2: Circle CenterX=15.65 CenterY=-10 CenterZ=0 NormalX=0 NormalY=0 NormalZ=1 AngleXU=0 Radius=1.5
    g3: Circle CenterX=15.65 CenterY=-31.5 CenterZ=0 NormalX=0 NormalY=0 NormalZ=1 AngleXU=0 Radius=1.5
    g4: Circle CenterX=15.65 CenterY=-56.5 CenterZ=0 NormalX=0 NormalY=0 NormalZ=1 AngleXU=0 Radius=1.5
    g5: LineSegment StartX=342.75 StartY=-10 StartZ=0 EndX=342.75 EndY=-31.5 EndZ=0
    g6: LineSegment StartX=342.75 StartY=-31.5 StartZ=0 EndX=342.75 EndY=-56.5 EndZ=0
    g7: Circle CenterX=342.75 CenterY=-10 CenterZ=0 NormalX=0 NormalY=0 NormalZ=1 AngleXU=0 Radius=1.5
    g8: Circle CenterX=342.75 CenterY=-31.5 CenterZ=0 NormalX=0 NormalY=0 NormalZ=1 AngleXU=0 Radius=1.5
    g9: Circle CenterX=342.75 CenterY=-56.5 CenterZ=0 NormalX=0 NormalY=0 NormalZ=1 AngleXU=0 Radius=1.5
  constraints (26):
    c: Vertical(g0)
    c: Coincident(g0,g1)
    c: Vertical(g1)
    c: Coincident(g2,g0)
    c: Coincident(g3,g0)
    c: Coincident(g4,g1)
    c: Equal(g4,g3)
    c: Equal(g3,g2)
    c: Distance(g1) = 25
    c: DistanceY(g0,g-1) = 10
    c: DistanceY(g1,g-1) = 56.5
    c: Radius(g2) = 1.5
    c: DistanceX(g-1,g0) = 15.65
    c: Vertical(g5)
    c: Coincident(g5,g6)
    c: Vertical(g6)
    c: Coincident(g7,g5)
    c: Coincident(g8,g5)
    c: Coincident(g9,g6)
    c: Equal(g9,g8)
    c: Equal(g8,g7)
    c: Equal(g1,g6) = 25
    c: Equal(g2,g7) = 1.5
    c: Horizontal(g9,g4)
    c: Horizontal(g7,g2)
    c: DistanceX(g-1,g7) = 342.75
FEATURE [PartDesign::Pocket] Pocket005
  BaseFeature = -> Pocket004
  Length = 5
  Length2 = 100
  Placement = pos=(0,0,0) rot=(0.57735,0.57735,0.57735;2.0944rad)
  Profile = -> Sketch006
  Type = 1
FEATURE [PartDesign::Body] OuterRightWall001
  Group = -> [LCS_0001,Sketch,Pad,Sketch001,Pocket,Sketch002,Pocket001,MultiTransform,LinearPattern,Sketch003,Pocket002,Sketch004,Pocket003,Sketch005,Pocket004,Sketch006,Pocket005]
  Origin = -> Origin001
  Tip = -> Pocket005
FEATURE [App::Part] OuterRightWall
  Group = -> [LCS_0,OuterRightWall001,PropertyBag]
  Origin = -> Origin
